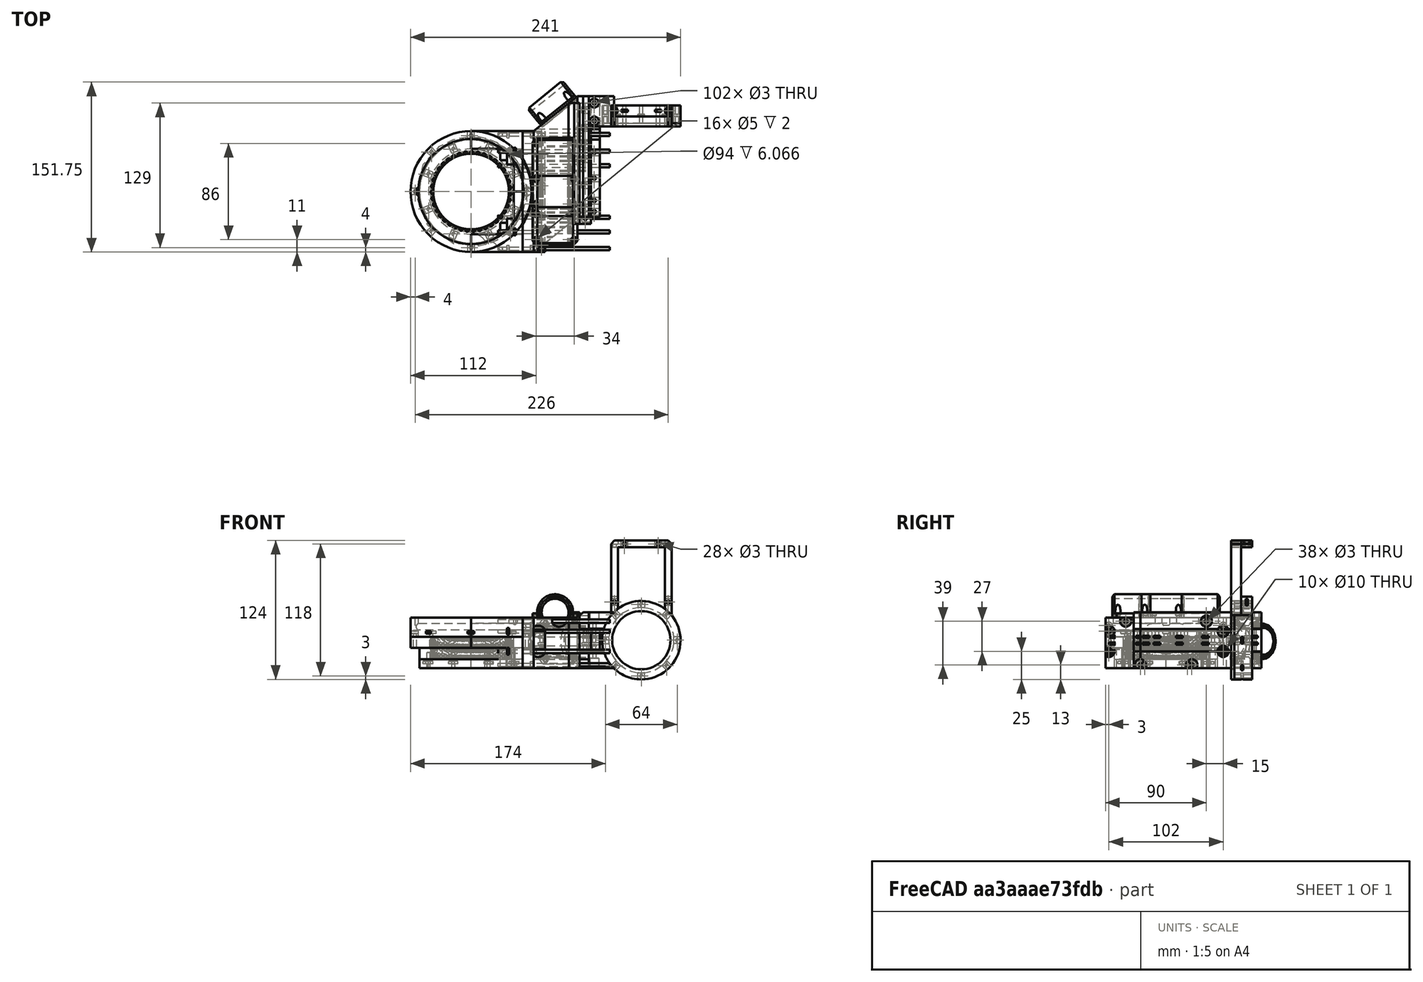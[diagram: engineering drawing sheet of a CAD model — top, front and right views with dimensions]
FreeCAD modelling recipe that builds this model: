
FCSTD DOCUMENT  (FreeCAD 0.19R24276 (Git))
Label: G-midi_adaptor-subshifted_022
License: All rights reserved
LicenseURL: http://en.wikipedia.org/wiki/All_rights_reserved
objects: Part::Cylinder×290, Part::Box×139, Part::Compound×113, Part::Cut×99, Part::Chamfer×16, Part::FeaturePython×11, Sketcher::SketchObject×2, Part::Extrusion×2, Part::Torus×2, Part::Fillet×2, Mesh::Feature×2, Part::Mirroring×1
note: 677 computed .brp shape members not serialized (recipe doc carries the construction recipe); baked Part::Feature solids carry a one-line shape summary decoded from their .brp

FEATURE [Part::Cylinder] Cylinder265  label="Válec265"
  Angle = 360
  AttacherType = Attacher::AttachEngine3D
  Height = 20
  Placement = pos=(45,19,-5) rot=(0,1,0;1.5708rad)
  Radius = 1.5
FEATURE [Part::Cylinder] Cylinder266  label="Válec266"
  Angle = 360
  AttacherType = Attacher::AttachEngine3D
  Height = 20
  Placement = pos=(45,-19,-5) rot=(0,1,0;1.5708rad)
  Radius = 1.5
FEATURE [Part::Cylinder] Cylinder267  label="Válec267"
  Angle = 360
  AttacherType = Attacher::AttachEngine3D
  Height = 20
  Placement = pos=(45,51,7) rot=(0,1,0;1.5708rad)
  Radius = 1.5
FEATURE [Part::Cylinder] Cylinder268  label="Válec268"
  Angle = 360
  AttacherType = Attacher::AttachEngine3D
  Height = 20
  Placement = pos=(45,-51,7) rot=(0,1,0;1.5708rad)
  Radius = 1.5
FEATURE [Part::Cylinder] Cylinder269  label="Válec269"
  Angle = 360
  AttacherType = Attacher::AttachEngine3D
  Height = 20
  Placement = pos=(45,-51,30) rot=(0,1,0;1.5708rad)
  Radius = 1.5
FEATURE [Part::Cylinder] Cylinder270  label="Válec270"
  Angle = 360
  AttacherType = Attacher::AttachEngine3D
  Height = 20
  Placement = pos=(45,51,30) rot=(0,1,0;1.5708rad)
  Radius = 1.5
FEATURE [Part::Cylinder] Cylinder271  label="Válec271"
  Angle = 360
  AttacherType = Attacher::AttachEngine3D
  Height = 28
  Placement = pos=(0,0,9) rot=(0,0,1;0rad)
  Radius = 54.5
FEATURE [Part::Box] Box117  label="Krychle117"
  AttacherType = Attacher::AttachEngine3D
  Height = 45
  Length = 10
  Placement = pos=(46,-54,-8) rot=(0,0,1;0rad)
  Width = 108
FEATURE [Part::Cylinder] Cylinder272  label="Válec272"
  Angle = 360
  AttacherType = Attacher::AttachEngine3D
  Height = 3
  Placement = pos=(53,51,30) rot=(0,1,0;1.5708rad)
  Radius = 3
FEATURE [Part::Cylinder] Cylinder273  label="Válec273"
  Angle = 360
  AttacherType = Attacher::AttachEngine3D
  Height = 3
  Placement = pos=(53,-51,30) rot=(0,1,0;1.5708rad)
  Radius = 3
FEATURE [Part::Cylinder] Cylinder274  label="Válec274"
  Angle = 360
  AttacherType = Attacher::AttachEngine3D
  Height = 3
  Placement = pos=(53,-51,7) rot=(0,1,0;1.5708rad)
  Radius = 3
FEATURE [Part::Cylinder] Cylinder275  label="Válec275"
  Angle = 360
  AttacherType = Attacher::AttachEngine3D
  Height = 3
  Placement = pos=(53,51,7) rot=(0,1,0;1.5708rad)
  Radius = 3
FEATURE [Part::Compound] Compound575
  Links = -> [Cylinder265,Cylinder266,Cylinder267,Cylinder268,Cylinder269,Cylinder270]
FEATURE [Part::Cylinder] Cylinder276  label="Válec276"
  Angle = 360
  AttacherType = Attacher::AttachEngine3D
  Height = 3
  Placement = pos=(53,-19,-5) rot=(0,1,0;1.5708rad)
  Radius = 3
FEATURE [Part::Cylinder] Cylinder277  label="Válec277"
  Angle = 360
  AttacherType = Attacher::AttachEngine3D
  Height = 3
  Placement = pos=(53,19,-5) rot=(0,1,0;1.5708rad)
  Radius = 3
FEATURE [Part::Compound] Compound576
  Links = -> [Cylinder277,Cylinder276,Cylinder275,Cylinder274,Cylinder273,Cylinder272]
FEATURE [Part::Cut] Cut348
  Base = -> Box117
  Tool = -> Compound576
FEATURE [Part::Cut] Cut349
  Base = -> Cut348
  Tool = -> Compound575
FEATURE [Part::Cut] Cut350
  Base = -> Cut349
  Tool = -> Cylinder271
FEATURE [Part::Cylinder] Cylinder278  label="Válec278"
  Angle = 360
  AttacherType = Attacher::AttachEngine3D
  Height = 50
  Placement = pos=(63,18,-12) rot=(0,0,1;0rad)
  Radius = 1.5
FEATURE [Part::Cylinder] Cylinder279  label="Válec279"
  Angle = 360
  AttacherType = Attacher::AttachEngine3D
  Height = 50
  Placement = pos=(63,33,-12) rot=(0,0,1;0rad)
  Radius = 1.5
FEATURE [Part::Cylinder] Cylinder280  label="Válec280"
  Angle = 360
  AttacherType = Attacher::AttachEngine3D
  Height = 50
  Placement = pos=(63,49,-12) rot=(0,0,1;0rad)
  Radius = 1.5
FEATURE [Part::Compound] Compound578
  Links = -> [Cylinder278,Cylinder279,Cylinder280]
FEATURE [Part::Box] Box118  label="Krychle118"
  AttacherType = Attacher::AttachEngine3D
  Height = 16
  Length = 10
  Placement = pos=(56,-54,6) rot=(0,0,1;0rad)
  Width = 108
FEATURE [Part::Box] Box119  label="Krychle119"
  AttacherType = Attacher::AttachEngine3D
  Height = 2
  Length = 6
  Placement = pos=(60,15,10) rot=(0,0,1;0rad)
  Width = 6
FEATURE [Part::Box] Box120  label="Krychle120"
  AttacherType = Attacher::AttachEngine3D
  Height = 2
  Length = 6
  Placement = pos=(60,30,10) rot=(0,0,1;0rad)
  Width = 6
FEATURE [Part::Box] Box121  label="Krychle121"
  AttacherType = Attacher::AttachEngine3D
  Height = 2
  Length = 6
  Placement = pos=(60,46,10) rot=(0,0,1;0rad)
  Width = 6
FEATURE [Part::Box] Box122  label="Krychle122"
  AttacherType = Attacher::AttachEngine3D
  Height = 2
  Length = 6
  Placement = pos=(60,15,16) rot=(0,0,1;0rad)
  Width = 6
FEATURE [Part::Box] Box123  label="Krychle123"
  AttacherType = Attacher::AttachEngine3D
  Height = 2
  Length = 6
  Placement = pos=(60,30,16) rot=(0,0,1;0rad)
  Width = 6
FEATURE [Part::Box] Box124  label="Krychle124"
  AttacherType = Attacher::AttachEngine3D
  Height = 2
  Length = 6
  Placement = pos=(60,46,16) rot=(0,0,1;0rad)
  Width = 6
FEATURE [Part::Compound] Compound577
  Links = -> [Box119,Box120,Box121,Box122,Box123,Box124]
FEATURE [Part::Cut] Cut351
  Base = -> Box118
  Tool = -> Compound577
FEATURE [Part::Cut] Cut352
  Base = -> Cut351
  Tool = -> Compound578
FEATURE [Part::Cylinder] Cylinder281  label="Válec281"
  Angle = 360
  AttacherType = Attacher::AttachEngine3D
  Height = 50
  Placement = pos=(63,5,-12) rot=(0,0,1;0rad)
  Radius = 1.5
FEATURE [Part::Cylinder] Cylinder282  label="Válec282"
  Angle = 360
  AttacherType = Attacher::AttachEngine3D
  Height = 50
  Placement = pos=(63,-22,-12) rot=(0,0,1;0rad)
  Radius = 1.5
FEATURE [Part::Cylinder] Cylinder283  label="Válec283"
  Angle = 360
  AttacherType = Attacher::AttachEngine3D
  Height = 50
  Placement = pos=(63,-33,-12) rot=(0,0,1;0rad)
  Radius = 1.5
FEATURE [Part::Cylinder] Cylinder284  label="Válec284"
  Angle = 360
  AttacherType = Attacher::AttachEngine3D
  Height = 50
  Placement = pos=(63,-48,-12) rot=(0,0,1;0rad)
  Radius = 1.5
FEATURE [Part::Compound] Compound580
  Links = -> [Cylinder281,Cylinder282,Cylinder283,Cylinder284]
FEATURE [Part::Box] Box125  label="Krychle125"
  AttacherType = Attacher::AttachEngine3D
  Height = 2
  Length = 6
  Placement = pos=(60,2,10) rot=(0,0,1;0rad)
  Width = 6
FEATURE [Part::Box] Box126  label="Krychle126"
  AttacherType = Attacher::AttachEngine3D
  Height = 2
  Length = 6
  Placement = pos=(60,2,16) rot=(0,0,1;0rad)
  Width = 6
FEATURE [Part::Box] Box127  label="Krychle127"
  AttacherType = Attacher::AttachEngine3D
  Height = 2
  Length = 6
  Placement = pos=(60,-25,10) rot=(0,0,1;0rad)
  Width = 6
FEATURE [Part::Box] Box128  label="Krychle128"
  AttacherType = Attacher::AttachEngine3D
  Height = 2
  Length = 6
  Placement = pos=(60,-25,16) rot=(0,0,1;0rad)
  Width = 6
FEATURE [Part::Box] Box129  label="Krychle129"
  AttacherType = Attacher::AttachEngine3D
  Height = 2
  Length = 6
  Placement = pos=(60,-36,10) rot=(0,0,1;0rad)
  Width = 6
FEATURE [Part::Box] Box130  label="Krychle130"
  AttacherType = Attacher::AttachEngine3D
  Height = 2
  Length = 6
  Placement = pos=(60,-36,16) rot=(0,0,1;0rad)
  Width = 6
FEATURE [Part::Box] Box131  label="Krychle131"
  AttacherType = Attacher::AttachEngine3D
  Height = 2
  Length = 6
  Placement = pos=(60,-51,10) rot=(0,0,1;0rad)
  Width = 6
FEATURE [Part::Box] Box132  label="Krychle132"
  AttacherType = Attacher::AttachEngine3D
  Height = 2
  Length = 6
  Placement = pos=(60,-51,16) rot=(0,0,1;0rad)
  Width = 6
FEATURE [Part::Compound] Compound579
  Links = -> [Box125,Box126,Box127,Box128,Box129,Box130,Box131,Box132]
FEATURE [Part::Cylinder] Cylinder285  label="Válec285"
  Angle = 360
  AttacherType = Attacher::AttachEngine3D
  Height = 16
  Placement = pos=(53,-51,7) rot=(0,1,0;1.5708rad)
  Radius = 3
FEATURE [Part::Cylinder] Cylinder286  label="Válec286"
  Angle = 360
  AttacherType = Attacher::AttachEngine3D
  Height = 16
  Placement = pos=(53,51,7) rot=(0,1,0;1.5708rad)
  Radius = 3
FEATURE [Part::Cylinder] Cylinder287  label="Válec287"
  Angle = 360
  AttacherType = Attacher::AttachEngine3D
  Height = 4
  Placement = pos=(50,0,5) rot=(0,0,1;0rad)
  Radius = 4
FEATURE [Part::Cut] Cut353
  Base = -> Cut352
  Tool = -> Compound579
FEATURE [Part::Cut] Cut354
  Base = -> Cut353
  Placement = pos=(0,0,3) rot=(0,0,1;0rad)
  Tool = -> Compound580
FEATURE [Part::Cut] Cut355
  Base = -> Cut354
  Tool = -> Cylinder285
FEATURE [Part::Cut] Cut356
  Base = -> Cut355
  Tool = -> Cylinder286
FEATURE [Part::Compound] Compound581  label="adapto_midi_podloch003"
  Links = -> [Cut356,Cut350]
FEATURE [Part::Cut] Cut357  label="G-midi_adaptor-high"
  Base = -> Compound581
  Tool = -> Cylinder287
FEATURE [Part::Cylinder] Cylinder288  label="Válec288"
  Angle = 360
  AttacherType = Attacher::AttachEngine3D
  Height = 20
  Placement = pos=(45,19,-5) rot=(0,1,0;1.5708rad)
  Radius = 1.5
FEATURE [Part::Cylinder] Cylinder289  label="Válec289"
  Angle = 360
  AttacherType = Attacher::AttachEngine3D
  Height = 20
  Placement = pos=(45,-19,-5) rot=(0,1,0;1.5708rad)
  Radius = 1.5
FEATURE [Part::Cylinder] Cylinder290  label="Válec290"
  Angle = 360
  AttacherType = Attacher::AttachEngine3D
  Height = 20
  Placement = pos=(45,51,7) rot=(0,1,0;1.5708rad)
  Radius = 1.5
FEATURE [Part::Cylinder] Cylinder291  label="Válec291"
  Angle = 360
  AttacherType = Attacher::AttachEngine3D
  Height = 20
  Placement = pos=(45,-51,7) rot=(0,1,0;1.5708rad)
  Radius = 1.5
FEATURE [Part::Cylinder] Cylinder292  label="Válec292"
  Angle = 360
  AttacherType = Attacher::AttachEngine3D
  Height = 20
  Placement = pos=(45,-51,30) rot=(0,1,0;1.5708rad)
  Radius = 1.5
FEATURE [Part::Cylinder] Cylinder293  label="Válec293"
  Angle = 360
  AttacherType = Attacher::AttachEngine3D
  Height = 20
  Placement = pos=(45,51,30) rot=(0,1,0;1.5708rad)
  Radius = 1.5
FEATURE [Part::Compound] Compound582
  Links = -> [Cylinder288,Cylinder289,Cylinder290,Cylinder291,Cylinder292,Cylinder293]
FEATURE [Part::Cylinder] Cylinder294  label="Válec294"
  Angle = 360
  AttacherType = Attacher::AttachEngine3D
  Height = 28
  Placement = pos=(0,0,9) rot=(0,0,1;0rad)
  Radius = 54.5
FEATURE [Part::Box] Box133  label="Krychle133"
  AttacherType = Attacher::AttachEngine3D
  Height = 45
  Length = 10
  Placement = pos=(46,-54,-8) rot=(0,0,1;0rad)
  Width = 108
FEATURE [Part::Cylinder] Cylinder295  label="Válec295"
  Angle = 360
  AttacherType = Attacher::AttachEngine3D
  Height = 3
  Placement = pos=(53,51,30) rot=(0,1,0;1.5708rad)
  Radius = 3
FEATURE [Part::Cylinder] Cylinder296  label="Válec296"
  Angle = 360
  AttacherType = Attacher::AttachEngine3D
  Height = 3
  Placement = pos=(53,-51,30) rot=(0,1,0;1.5708rad)
  Radius = 3
FEATURE [Part::Cylinder] Cylinder297  label="Válec297"
  Angle = 360
  AttacherType = Attacher::AttachEngine3D
  Height = 3
  Placement = pos=(53,-51,7) rot=(0,1,0;1.5708rad)
  Radius = 3
FEATURE [Part::Cylinder] Cylinder298  label="Válec298"
  Angle = 360
  AttacherType = Attacher::AttachEngine3D
  Height = 3
  Placement = pos=(53,51,7) rot=(0,1,0;1.5708rad)
  Radius = 3
FEATURE [Part::Cylinder] Cylinder299  label="Válec299"
  Angle = 360
  AttacherType = Attacher::AttachEngine3D
  Height = 3
  Placement = pos=(53,-19,-5) rot=(0,1,0;1.5708rad)
  Radius = 3
FEATURE [Part::Cylinder] Cylinder300  label="Válec300"
  Angle = 360
  AttacherType = Attacher::AttachEngine3D
  Height = 3
  Placement = pos=(53,19,-5) rot=(0,1,0;1.5708rad)
  Radius = 3
FEATURE [Part::Compound] Compound583
  Links = -> [Cylinder300,Cylinder299,Cylinder298,Cylinder297,Cylinder296,Cylinder295]
FEATURE [Part::Cut] Cut358
  Base = -> Box133
  Tool = -> Compound583
FEATURE [Part::Cut] Cut360
  Base = -> Cut358
  Tool = -> Compound582
FEATURE [Part::Cut] Cut359
  Base = -> Cut360
  Tool = -> Cylinder294
FEATURE [Sketcher::SketchObject] Sketch
  FullyConstrained = true
  Placement = pos=(0,-54,-8) rot=(0.57735,0.57735,0.57735;2.0944rad)
  sketch-geometry (4):
    g0: LineSegment StartX=0 StartY=0 StartZ=0 EndX=108 EndY=0 EndZ=0
    g1: LineSegment StartX=108 StartY=0 StartZ=0 EndX=108 EndY=45 EndZ=0
    g2: LineSegment StartX=108 StartY=45 StartZ=0 EndX=0 EndY=45 EndZ=0
    g3: LineSegment StartX=0 StartY=45 StartZ=0 EndX=0 EndY=0 EndZ=0
  constraints (11):
    c: Coincident(g0,g1)
    c: Coincident(g1,g2)
    c: Coincident(g2,g3)
    c: Coincident(g3,g0)
    c: Horizontal(g0)
    c: Horizontal(g2)
    c: Vertical(g1)
    c: Vertical(g3)
    c: Distance(g1) = 45
    c: Distance(g2) = 108
    c: Coincident(g-1,g0)
FEATURE [Part::Extrusion] Extrude
  Base = -> Sketch
  Dir = (1,0.8,0)
  DirMode = 0
  FaceMakerClass = Part::FaceMakerBullseye
  LengthFwd = 40
  LengthRev = 0
  Placement = pos=(56,0,0) rot=(0,0,1;0rad)
  Solid = true
  Symmetric = false
FEATURE [Part::Box] Box134  label="Krychle134"
  AttacherType = Attacher::AttachEngine3D
  Height = 50
  Length = 10
  Placement = pos=(87,-29,-8) rot=(0,0,1;0rad)
  Width = 108
FEATURE [Part::Torus] Torus004  label="Anuloid004"
  Angle1 = -180
  Angle2 = 180
  Angle3 = 360
  AttacherType = Attacher::AttachEngine3D
  Placement = pos=(0,0,29) rot=(0,0,1;0rad)
  Radius1 = 46
  Radius2 = 3.1
FEATURE [Part::Torus] Torus005  label="Anuloid005"
  Angle1 = -180
  Angle2 = 180
  Angle3 = 360
  AttacherType = Attacher::AttachEngine3D
  Placement = pos=(0,0,29) rot=(0,0,1;0rad)
  Radius1 = 46
  Radius2 = 3.1
FEATURE [Part::FeaturePython] wormgear024  # WARN: FeaturePython — macro-defined, semantics opaque (R4)
  AttacherType = Attacher::AttachEngine3D
  beta = 29.0893
  clearance = 0.25
  diameter = 70.1
  head = 0
  height = 20
  module = 1
  pressure_angle = 20
  reverse_pitch = false
  teeth = 39
  version = 0.0.3
FEATURE [Part::FeaturePython] wormgear025  # WARN: FeaturePython — macro-defined, semantics opaque (R4)
  AttacherType = Attacher::AttachEngine3D
  Placement = pos=(0,0,0) rot=(0,0,-1;0.005411rad)
  beta = 29.0893
  clearance = 0.25
  diameter = 70.1
  head = 0
  height = 20
  module = 1
  pressure_angle = 20
  reverse_pitch = true
  teeth = 39
  version = 0.0.3
FEATURE [Part::Cylinder] Cylinder113  label="Válec113"
  Angle = 360
  AttacherType = Attacher::AttachEngine3D
  Height = 10
  Radius = 54
FEATURE [Part::Cut] Cut063
  Base = -> Cylinder113
  Placement = pos=(0,0,10) rot=(0,0,1;0.034907rad)
  Tool = -> wormgear025
FEATURE [Part::Cylinder] Cylinder114  label="Válec114"
  Angle = 360
  AttacherType = Attacher::AttachEngine3D
  Height = 10
  Radius = 46
FEATURE [Part::Cut] Cut062
  Base = -> Cylinder114
  Tool = -> wormgear024
FEATURE [Part::Compound] Compound191
  Links = -> [Cut063,Cut062]
FEATURE [Part::Box] Box070  label="Krychle070"
  AttacherType = Attacher::AttachEngine3D
  Height = 2
  Length = 8
  Placement = pos=(37,-3,-4) rot=(0,0,1;0rad)
  Width = 6
FEATURE [Part::FeaturePython] Tube009  # WARN: FeaturePython — macro-defined, semantics opaque (R4)
  AttacherType = Attacher::AttachEngine3D
  Height = 8
  InnerRadius = 38
  OuterRadius = 46
  Placement = pos=(0,0,-8) rot=(0,0,1;0rad)
FEATURE [Part::Cylinder] Cylinder189  label="Válec189"
  Angle = 360
  AttacherType = Attacher::AttachEngine3D
  Height = 60
  Placement = pos=(41,0,-54) rot=(0,0,1;0rad)
  Radius = 1.5
FEATURE [Part::Cylinder] Cylinder190  label="Válec190"
  Angle = 360
  AttacherType = Attacher::AttachEngine3D
  Height = 40
  Placement = pos=(256,0,-30) rot=(0,0,1;0rad)
  Radius = 10
FEATURE [Part::Box] Box071  label="Krychle071"
  AttacherType = Attacher::AttachEngine3D
  Height = 28
  Length = 8
  Placement = pos=(238,0,-8) rot=(0,0,1;0rad)
  Width = 38
FEATURE [Part::Cylinder] Cylinder191  label="Válec191"
  Angle = 360
  AttacherType = Attacher::AttachEngine3D
  Height = 40
  Placement = pos=(214,56,-30) rot=(0,0,1;0rad)
  Radius = 12
FEATURE [Part::Compound] Compound193
  Links = -> [Cylinder190,Cylinder191]
FEATURE [Part::Box] Box072  label="Krychle072"
  AttacherType = Attacher::AttachEngine3D
  Height = 28
  Length = 46
  Placement = pos=(200,38,-8) rot=(0,0,1;0rad)
  Width = 16
FEATURE [Part::Compound] Compound192
  Links = -> [Box071,Box072]
FEATURE [Part::Cut] Cut065
  Base = -> Compound192
  Tool = -> Compound193
FEATURE [Part::Cylinder] Cylinder192  label="Válec192"
  Angle = 360
  AttacherType = Attacher::AttachEngine3D
  Height = 40
  Placement = pos=(202,50,-30) rot=(0,0,1;0rad)
  Radius = 12
FEATURE [Part::Cut] Cut066
  Base = -> Cut065
  Placement = pos=(-200,0,0) rot=(0,0,1;0rad)
  Tool = -> Cylinder192
FEATURE [Part::Box] Box073  label="Krychle073"
  AttacherType = Attacher::AttachEngine3D
  Height = 28
  Length = 6
  Placement = pos=(26,28,-8) rot=(0,0,1;0rad)
  Width = 10
FEATURE [Part::Box] Box074  label="Krychle074"
  AttacherType = Attacher::AttachEngine3D
  Height = 28
  Length = 6
  Placement = pos=(32,24,-8) rot=(0,0,1;0rad)
  Width = 14
FEATURE [Part::Compound] Compound
  Links = -> [Box073,Box074]
FEATURE [Part::Compound] Compound194
  Links = -> [Cut066,Compound]
FEATURE [Part::Box] Box075  label="Krychle075"
  AttacherType = Attacher::AttachEngine3D
  Height = 28
  Length = 8
  Placement = pos=(238,0,-8) rot=(0,0,1;0rad)
  Width = 38
FEATURE [Part::Cylinder] Cylinder193  label="Válec193"
  Angle = 360
  AttacherType = Attacher::AttachEngine3D
  Height = 40
  Placement = pos=(214,56,-30) rot=(0,0,1;0rad)
  Radius = 12
FEATURE [Part::Cylinder] Cylinder194  label="Válec194"
  Angle = 360
  AttacherType = Attacher::AttachEngine3D
  Height = 40
  Placement = pos=(256,0,-30) rot=(0,0,1;0rad)
  Radius = 10
FEATURE [Part::Compound] Compound198
  Links = -> [Cylinder194,Cylinder193]
FEATURE [Part::Box] Box076  label="Krychle076"
  AttacherType = Attacher::AttachEngine3D
  Height = 28
  Length = 6
  Placement = pos=(26,28,-8) rot=(0,0,1;0rad)
  Width = 10
FEATURE [Part::Cylinder] Cylinder195  label="Válec195"
  Angle = 360
  AttacherType = Attacher::AttachEngine3D
  Height = 40
  Placement = pos=(202,50,-30) rot=(0,0,1;0rad)
  Radius = 12
FEATURE [Part::Box] Box077  label="Krychle077"
  AttacherType = Attacher::AttachEngine3D
  Height = 28
  Length = 6
  Placement = pos=(32,24,-8) rot=(0,0,1;0rad)
  Width = 14
FEATURE [Part::Compound] Compound195
  Links = -> [Box076,Box077]
FEATURE [Part::Box] Box078  label="Krychle078"
  AttacherType = Attacher::AttachEngine3D
  Height = 28
  Length = 46
  Placement = pos=(200,38,-8) rot=(0,0,1;0rad)
  Width = 16
FEATURE [Part::Compound] Compound197
  Links = -> [Box075,Box078]
FEATURE [Part::Cut] Cut068
  Base = -> Compound197
  Tool = -> Compound198
FEATURE [Part::Cut] Cut067
  Base = -> Cut068
  Placement = pos=(-200,0,0) rot=(0,0,1;0rad)
  Tool = -> Cylinder195
FEATURE [Part::Compound] Compound196
  Links = -> [Cut067,Compound195]
FEATURE [Part::Mirroring] mirror  label="Compound196 (mirrored)"
  Base = (0,0,0)
  Normal = (1e-16,-1,0)
  Source = -> Compound196
FEATURE [Part::Box] Box087  label="Krychle087"
  AttacherType = Attacher::AttachEngine3D
  Height = 2
  Length = 8
  Placement = pos=(28.2843,24.0416,-4) rot=(0,0,1;0.785398rad)
  Width = 6
FEATURE [Part::Box] Box088  label="Krychle088"
  AttacherType = Attacher::AttachEngine3D
  Height = 2
  Length = 8
  Placement = pos=(3,37,-4) rot=(0,0,1;1.5708rad)
  Width = 6
FEATURE [Part::Box] Box089  label="Krychle089"
  AttacherType = Attacher::AttachEngine3D
  Height = 2
  Length = 8
  Placement = pos=(-24.0416,28.2843,-4) rot=(0,0,1;2.35619rad)
  Width = 6
FEATURE [Part::Box] Box090  label="Krychle090"
  AttacherType = Attacher::AttachEngine3D
  Height = 2
  Length = 8
  Placement = pos=(-37,3,-4) rot=(0,0,1;3.14159rad)
  Width = 6
FEATURE [Part::Box] Box091  label="Krychle091"
  AttacherType = Attacher::AttachEngine3D
  Height = 2
  Length = 8
  Placement = pos=(-28.2843,-24.0416,-4) rot=(0,0,1;3.92699rad)
  Width = 6
FEATURE [Part::Box] Box092  label="Krychle092"
  AttacherType = Attacher::AttachEngine3D
  Height = 2
  Length = 8
  Placement = pos=(-3,-37,-4) rot=(0,0,-1;1.5708rad)
  Width = 6
FEATURE [Part::Box] Box093  label="Krychle093"
  AttacherType = Attacher::AttachEngine3D
  Height = 2
  Length = 8
  Placement = pos=(24.0416,-28.2843,-4) rot=(0,0,-1;0.785398rad)
  Width = 6
FEATURE [Part::Cylinder] Cylinder204  label="Válec204"
  Angle = 360
  AttacherType = Attacher::AttachEngine3D
  Height = 60
  Placement = pos=(28.9914,28.9914,-54) rot=(0,0,1;0.785398rad)
  Radius = 1.5
FEATURE [Part::Cylinder] Cylinder205  label="Válec205"
  Angle = 360
  AttacherType = Attacher::AttachEngine3D
  Height = 60
  Placement = pos=(-4e-15,41,-54) rot=(0,0,1;1.5708rad)
  Radius = 1.5
FEATURE [Part::Cylinder] Cylinder206  label="Válec206"
  Angle = 360
  AttacherType = Attacher::AttachEngine3D
  Height = 60
  Placement = pos=(-28.9914,28.9914,-54) rot=(0,0,1;2.35619rad)
  Radius = 1.5
FEATURE [Part::Cylinder] Cylinder207  label="Válec207"
  Angle = 360
  AttacherType = Attacher::AttachEngine3D
  Height = 60
  Placement = pos=(-41,-1.1e-14,-54) rot=(0,0,1;3.14159rad)
  Radius = 1.5
FEATURE [Part::Compound] Compound206
  Links = -> [Box087,Box088,Box089,Box090,Box091,Box092,Box093,Box070]
  Placement = pos=(0,0,0) rot=(0,0,1;0.392699rad)
FEATURE [Part::Compound] Compound210
  Links = -> [mirror,Compound194]
FEATURE [Part::Cylinder] Cylinder208  label="Válec208"
  Angle = 360
  AttacherType = Attacher::AttachEngine3D
  Height = 60
  Placement = pos=(-28.9914,-28.9914,-54) rot=(0,0,1;3.92699rad)
  Radius = 1.5
FEATURE [Part::Cylinder] Cylinder209  label="Válec209"
  Angle = 360
  AttacherType = Attacher::AttachEngine3D
  Height = 60
  Placement = pos=(1.2e-14,-41,-54) rot=(0,0,-1;1.5708rad)
  Radius = 1.5
FEATURE [Part::Cylinder] Cylinder210  label="Válec210"
  Angle = 360
  AttacherType = Attacher::AttachEngine3D
  Height = 60
  Placement = pos=(28.9914,-28.9914,-54) rot=(0,0,-1;0.785398rad)
  Radius = 1.5
FEATURE [Part::Compound] Compound207
  Links = -> [Cylinder204,Cylinder205,Cylinder206,Cylinder207,Cylinder208,Cylinder209,Cylinder210,Cylinder189]
  Placement = pos=(0,0,0) rot=(0,0,1;0.392699rad)
FEATURE [Part::Cut] Cut069
  Base = -> Tube009
  Tool = -> Compound207
FEATURE [Part::Cut] Cut070
  Base = -> Cut069
  Tool = -> Compound206
FEATURE [Part::Cylinder] Cylinder211  label="Válec211"
  Angle = 360
  AttacherType = Attacher::AttachEngine3D
  Height = 60
  Placement = pos=(28.9914,-28.9914,-54) rot=(0,0,-1;0.785398rad)
  Radius = 1.5
FEATURE [Part::Cylinder] Cylinder212  label="Válec212"
  Angle = 360
  AttacherType = Attacher::AttachEngine3D
  Height = 60
  Placement = pos=(-4e-15,41,-54) rot=(0,0,1;1.5708rad)
  Radius = 1.5
FEATURE [Part::Cylinder] Cylinder213  label="Válec213"
  Angle = 360
  AttacherType = Attacher::AttachEngine3D
  Height = 60
  Placement = pos=(-28.9914,28.9914,-54) rot=(0,0,1;2.35619rad)
  Radius = 1.5
FEATURE [Part::Cylinder] Cylinder214  label="Válec214"
  Angle = 360
  AttacherType = Attacher::AttachEngine3D
  Height = 60
  Placement = pos=(28.9914,28.9914,-54) rot=(0,0,1;0.785398rad)
  Radius = 1.5
FEATURE [Part::Cylinder] Cylinder215  label="Válec215"
  Angle = 360
  AttacherType = Attacher::AttachEngine3D
  Height = 60
  Placement = pos=(-41,-1.1e-14,-54) rot=(0,0,1;3.14159rad)
  Radius = 1.5
FEATURE [Part::Cylinder] Cylinder216  label="Válec216"
  Angle = 360
  AttacherType = Attacher::AttachEngine3D
  Height = 60
  Placement = pos=(-28.9914,-28.9914,-54) rot=(0,0,1;3.92699rad)
  Radius = 1.5
FEATURE [Part::Cylinder] Cylinder217  label="Válec217"
  Angle = 360
  AttacherType = Attacher::AttachEngine3D
  Height = 60
  Placement = pos=(1.2e-14,-41,-54) rot=(0,0,-1;1.5708rad)
  Radius = 1.5
FEATURE [Part::Cylinder] Cylinder218  label="Válec218"
  Angle = 360
  AttacherType = Attacher::AttachEngine3D
  Height = 60
  Placement = pos=(41,0,-54) rot=(0,0,1;0rad)
  Radius = 1.5
FEATURE [Part::Compound] Compound208
  Links = -> [Cylinder214,Cylinder212,Cylinder213,Cylinder215,Cylinder216,Cylinder217,Cylinder211,Cylinder218]
  Placement = pos=(0,0,0) rot=(0,0,1;0.392699rad)
FEATURE [Part::Box] Box094  label="Krychle094"
  AttacherType = Attacher::AttachEngine3D
  Height = 2
  Length = 8
  Placement = pos=(3,37,-4) rot=(0,0,1;1.5708rad)
  Width = 6
FEATURE [Part::Box] Box095  label="Krychle095"
  AttacherType = Attacher::AttachEngine3D
  Height = 2
  Length = 8
  Placement = pos=(28.2843,24.0416,-4) rot=(0,0,1;0.785398rad)
  Width = 6
FEATURE [Part::Box] Box096  label="Krychle096"
  AttacherType = Attacher::AttachEngine3D
  Height = 2
  Length = 8
  Placement = pos=(24.0416,-28.2843,-4) rot=(0,0,-1;0.785398rad)
  Width = 6
FEATURE [Part::Box] Box097  label="Krychle097"
  AttacherType = Attacher::AttachEngine3D
  Height = 2
  Length = 8
  Placement = pos=(-37,3,-4) rot=(0,0,1;3.14159rad)
  Width = 6
FEATURE [Part::Box] Box098  label="Krychle098"
  AttacherType = Attacher::AttachEngine3D
  Height = 2
  Length = 8
  Placement = pos=(-28.2843,-24.0416,-4) rot=(0,0,1;3.92699rad)
  Width = 6
FEATURE [Part::Box] Box099  label="Krychle099"
  AttacherType = Attacher::AttachEngine3D
  Height = 2
  Length = 8
  Placement = pos=(-3,-37,-4) rot=(0,0,-1;1.5708rad)
  Width = 6
FEATURE [Part::Box] Box100  label="Krychle100"
  AttacherType = Attacher::AttachEngine3D
  Height = 2
  Length = 8
  Placement = pos=(-24.0416,28.2843,-4) rot=(0,0,1;2.35619rad)
  Width = 6
FEATURE [Part::Box] Box101  label="Krychle101"
  AttacherType = Attacher::AttachEngine3D
  Height = 2
  Length = 8
  Placement = pos=(37,-3,-4) rot=(0,0,1;0rad)
  Width = 6
FEATURE [Part::Compound] Compound209
  Links = -> [Box095,Box094,Box100,Box097,Box098,Box099,Box096,Box101]
  Placement = pos=(0,0,0) rot=(0,0,1;0.392699rad)
FEATURE [Part::Cylinder] Cylinder219  label="Válec219"
  Angle = 360
  AttacherType = Attacher::AttachEngine3D
  Height = 60
  Placement = pos=(28.9914,-28.9914,-54) rot=(0,0,-1;0.785398rad)
  Radius = 1.5
FEATURE [Part::Cylinder] Cylinder220  label="Válec220"
  Angle = 360
  AttacherType = Attacher::AttachEngine3D
  Height = 60
  Placement = pos=(-28.9914,28.9914,-54) rot=(0,0,1;2.35619rad)
  Radius = 1.5
FEATURE [Part::Cylinder] Cylinder221  label="Válec221"
  Angle = 360
  AttacherType = Attacher::AttachEngine3D
  Height = 60
  Placement = pos=(28.9914,28.9914,-54) rot=(0,0,1;0.785398rad)
  Radius = 1.5
FEATURE [Part::Cylinder] Cylinder222  label="Válec222"
  Angle = 360
  AttacherType = Attacher::AttachEngine3D
  Height = 60
  Placement = pos=(-4e-15,41,-54) rot=(0,0,1;1.5708rad)
  Radius = 1.5
FEATURE [Part::Cylinder] Cylinder223  label="Válec223"
  Angle = 360
  AttacherType = Attacher::AttachEngine3D
  Height = 60
  Placement = pos=(41,0,-54) rot=(0,0,1;0rad)
  Radius = 1.5
FEATURE [Part::Cut] Cut071
  Base = -> Compound210
  Tool = -> Compound209
FEATURE [Part::Cut] Cut072
  Base = -> Cut071
  Tool = -> Compound208
FEATURE [Part::Cylinder] Cylinder224  label="Válec224"
  Angle = 360
  AttacherType = Attacher::AttachEngine3D
  Height = 60
  Placement = pos=(-28.9914,-28.9914,-54) rot=(0,0,1;3.92699rad)
  Radius = 1.5
FEATURE [Part::Cylinder] Cylinder225  label="Válec225"
  Angle = 360
  AttacherType = Attacher::AttachEngine3D
  Height = 60
  Placement = pos=(-41,-1.1e-14,-54) rot=(0,0,1;3.14159rad)
  Radius = 1.5
FEATURE [Part::Cylinder] Cylinder226  label="Válec226"
  Angle = 360
  AttacherType = Attacher::AttachEngine3D
  Height = 60
  Placement = pos=(1.2e-14,-41,-54) rot=(0,0,-1;1.5708rad)
  Radius = 1.5
FEATURE [Part::Compound] Compound211
  Links = -> [Cylinder221,Cylinder222,Cylinder220,Cylinder225,Cylinder224,Cylinder226,Cylinder219,Cylinder223]
  Placement = pos=(0,0,0) rot=(0,0,1;0.392699rad)
FEATURE [Part::Cut] Cut073
  Base = -> Compound191
  Tool = -> Compound211
FEATURE [Part::Cylinder] Cylinder227  label="Válec227"
  Angle = 360
  AttacherType = Attacher::AttachEngine3D
  Height = 60
  Placement = pos=(28,-51,7) rot=(0,1,0;1.5708rad)
  Radius = 1.5
FEATURE [Part::Cylinder] Cylinder228  label="Válec228"
  Angle = 360
  AttacherType = Attacher::AttachEngine3D
  Height = 60
  Placement = pos=(28,51,7) rot=(0,1,0;1.5708rad)
  Radius = 1.5
FEATURE [Part::Cylinder] Cylinder229  label="Válec229"
  Angle = 360
  AttacherType = Attacher::AttachEngine3D
  Height = 60
  Placement = pos=(32,21,-5) rot=(0,1,0;1.5708rad)
  Radius = 1.5
FEATURE [Part::Cylinder] Cylinder230  label="Válec230"
  Angle = 360
  AttacherType = Attacher::AttachEngine3D
  Height = 60
  Placement = pos=(32,-21,-5) rot=(0,1,0;1.5708rad)
  Radius = 1.5
FEATURE [Part::Compound] Compound212
  Links = -> [Cylinder229,Cylinder230,Cylinder228,Cylinder227]
FEATURE [Part::Cut] Cut074
  Base = -> Cut073
  Tool = -> Compound212
FEATURE [Part::Box] Box102  label="Krychle102"
  AttacherType = Attacher::AttachEngine3D
  Height = 6
  Length = 2
  Placement = pos=(36,18,-8) rot=(0,0,1;0rad)
  Width = 6
FEATURE [Part::Box] Box103  label="Krychle103"
  AttacherType = Attacher::AttachEngine3D
  Height = 6
  Length = 2
  Placement = pos=(36,-24,-8) rot=(0,0,1;0rad)
  Width = 6
FEATURE [Part::Box] Box104  label="Krychle104"
  AttacherType = Attacher::AttachEngine3D
  Height = 6
  Length = 2
  Placement = pos=(32,-54,4) rot=(0,0,1;0rad)
  Width = 6
FEATURE [Part::Box] Box105  label="Krychle105"
  AttacherType = Attacher::AttachEngine3D
  Height = 6
  Length = 2
  Placement = pos=(32,48,4) rot=(0,0,1;0rad)
  Width = 6
FEATURE [Part::Compound] Compound213
  Links = -> [Box102,Box103,Box105,Box104]
FEATURE [Part::Cut] Cut075
  Base = -> Cut074
  Tool = -> Compound213
FEATURE [Part::Cylinder] Cylinder239  label="Válec239"
  Angle = 360
  AttacherType = Attacher::AttachEngine3D
  Height = 50
  Placement = pos=(50,0,-15) rot=(0,0,1;0rad)
  Radius = 1.5
FEATURE [Part::Cylinder] Cylinder240  label="Válec240"
  Angle = 360
  AttacherType = Attacher::AttachEngine3D
  Height = 50
  Placement = pos=(35.3553,35.3553,-15) rot=(0,0,1;0.785398rad)
  Radius = 1.5
FEATURE [Part::Cylinder] Cylinder241  label="Válec241"
  Angle = 360
  AttacherType = Attacher::AttachEngine3D
  Height = 50
  Placement = pos=(-7e-15,50,-15) rot=(0,0,1;1.5708rad)
  Radius = 1.5
FEATURE [Part::Cylinder] Cylinder242  label="Válec242"
  Angle = 360
  AttacherType = Attacher::AttachEngine3D
  Height = 50
  Placement = pos=(-35.3553,35.3553,-15) rot=(0,0,1;2.35619rad)
  Radius = 1.5
FEATURE [Part::Cylinder] Cylinder243  label="Válec243"
  Angle = 360
  AttacherType = Attacher::AttachEngine3D
  Height = 50
  Placement = pos=(-50,-2.3e-14,-15) rot=(0,0,1;3.14159rad)
  Radius = 1.5
FEATURE [Part::Cylinder] Cylinder244  label="Válec244"
  Angle = 360
  AttacherType = Attacher::AttachEngine3D
  Height = 50
  Placement = pos=(-35.3553,-35.3553,-15) rot=(0,0,1;3.92699rad)
  Radius = 1.5
FEATURE [Part::Cylinder] Cylinder245  label="Válec245"
  Angle = 360
  AttacherType = Attacher::AttachEngine3D
  Height = 50
  Placement = pos=(2.5e-14,-50,-15) rot=(0,0,-1;1.5708rad)
  Radius = 1.5
FEATURE [Part::Cylinder] Cylinder246  label="Válec246"
  Angle = 360
  AttacherType = Attacher::AttachEngine3D
  Height = 50
  Placement = pos=(35.3553,-35.3553,-15) rot=(0,0,-1;0.785398rad)
  Radius = 1.5
FEATURE [Part::Compound] Compound217
  Links = -> [Cylinder239,Cylinder240,Cylinder241,Cylinder242,Cylinder243,Cylinder244,Cylinder245,Cylinder246]
FEATURE [Part::Cut] Cut076
  Base = -> Cut075
  Tool = -> Compound217
FEATURE [Part::Box] Box106  label="Krychle106"
  AttacherType = Attacher::AttachEngine3D
  Height = 6
  Length = 2
  Placement = pos=(36,-26,-8) rot=(0,0,1;0rad)
  Width = 6
FEATURE [Part::Box] Box107  label="Krychle107"
  AttacherType = Attacher::AttachEngine3D
  Height = 6
  Length = 2
  Placement = pos=(32,-54,4) rot=(0,0,1;0rad)
  Width = 6
FEATURE [Part::Box] Box108  label="Krychle108"
  AttacherType = Attacher::AttachEngine3D
  Height = 6
  Length = 2
  Placement = pos=(36,20,-8) rot=(0,0,1;0rad)
  Width = 6
FEATURE [Part::Box] Box109  label="Krychle109"
  AttacherType = Attacher::AttachEngine3D
  Height = 6
  Length = 2
  Placement = pos=(32,48,4) rot=(0,0,1;0rad)
  Width = 6
FEATURE [Part::Compound] Compound218
  Links = -> [Box108,Box106,Box109,Box107]
FEATURE [Part::Cut] Cut080
  Base = -> Cut070
  Tool = -> Compound218
FEATURE [Part::Cylinder] Cylinder247  label="Válec247"
  Angle = 360
  AttacherType = Attacher::AttachEngine3D
  Height = 60
  Placement = pos=(32,-23,-5) rot=(0,1,0;1.5708rad)
  Radius = 1.5
FEATURE [Part::Cylinder] Cylinder248  label="Válec248"
  Angle = 360
  AttacherType = Attacher::AttachEngine3D
  Height = 60
  Placement = pos=(28,51,7) rot=(0,1,0;1.5708rad)
  Radius = 1.5
FEATURE [Part::Cylinder] Cylinder249  label="Válec249"
  Angle = 360
  AttacherType = Attacher::AttachEngine3D
  Height = 60
  Placement = pos=(32,23,-5) rot=(0,1,0;1.5708rad)
  Radius = 1.5
FEATURE [Part::Cylinder] Cylinder250  label="Válec250"
  Angle = 360
  AttacherType = Attacher::AttachEngine3D
  Height = 60
  Placement = pos=(28,-51,7) rot=(0,1,0;1.5708rad)
  Radius = 1.5
FEATURE [Part::Compound] Compound219
  Links = -> [Cylinder249,Cylinder247,Cylinder248,Cylinder250]
FEATURE [Part::Cylinder] Cylinder251  label="Válec251"
  Angle = 360
  AttacherType = Attacher::AttachEngine3D
  Height = 50
  Placement = pos=(35.3553,35.3553,-15) rot=(0,0,1;0.785398rad)
  Radius = 1.5
FEATURE [Part::Cylinder] Cylinder252  label="Válec252"
  Angle = 360
  AttacherType = Attacher::AttachEngine3D
  Height = 50
  Placement = pos=(50,0,-15) rot=(0,0,1;0rad)
  Radius = 1.5
FEATURE [Part::Cylinder] Cylinder253  label="Válec253"
  Angle = 360
  AttacherType = Attacher::AttachEngine3D
  Height = 50
  Placement = pos=(35.3553,-35.3553,-15) rot=(0,0,-1;0.785398rad)
  Radius = 1.5
FEATURE [Part::Cylinder] Cylinder254  label="Válec254"
  Angle = 360
  AttacherType = Attacher::AttachEngine3D
  Height = 50
  Placement = pos=(-50,-2.3e-14,-15) rot=(0,0,1;3.14159rad)
  Radius = 1.5
FEATURE [Part::Cylinder] Cylinder255  label="Válec255"
  Angle = 360
  AttacherType = Attacher::AttachEngine3D
  Height = 50
  Placement = pos=(2.5e-14,-50,-15) rot=(0,0,-1;1.5708rad)
  Radius = 1.5
FEATURE [Part::Cylinder] Cylinder256  label="Válec256"
  Angle = 360
  AttacherType = Attacher::AttachEngine3D
  Height = 50
  Placement = pos=(-35.3553,35.3553,-15) rot=(0,0,1;2.35619rad)
  Radius = 1.5
FEATURE [Part::Cylinder] Cylinder257  label="Válec257"
  Angle = 360
  AttacherType = Attacher::AttachEngine3D
  Height = 50
  Placement = pos=(-7e-15,50,-15) rot=(0,0,1;1.5708rad)
  Radius = 1.5
FEATURE [Part::Cylinder] Cylinder258  label="Válec258"
  Angle = 360
  AttacherType = Attacher::AttachEngine3D
  Height = 50
  Placement = pos=(-35.3553,-35.3553,-15) rot=(0,0,1;3.92699rad)
  Radius = 1.5
FEATURE [Part::Box] Box110  label="Krychle110"
  AttacherType = Attacher::AttachEngine3D
  Height = 6
  Length = 2
  Placement = pos=(36,20,-8) rot=(0,0,1;0rad)
  Width = 6
FEATURE [Part::Compound] Compound220
  Links = -> [Cylinder252,Cylinder251,Cylinder257,Cylinder256,Cylinder254,Cylinder258,Cylinder255,Cylinder253]
FEATURE [Part::Cut] Cut077
  Base = -> Cut072
  Tool = -> Compound220
FEATURE [Part::Box] Box111  label="Krychle111"
  AttacherType = Attacher::AttachEngine3D
  Height = 6
  Length = 2
  Placement = pos=(32,-54,4) rot=(0,0,1;0rad)
  Width = 6
FEATURE [Part::Box] Box112  label="Krychle112"
  AttacherType = Attacher::AttachEngine3D
  Height = 6
  Length = 2
  Placement = pos=(36,-26,-8) rot=(0,0,1;0rad)
  Width = 6
FEATURE [Part::Box] Box113  label="Krychle113"
  AttacherType = Attacher::AttachEngine3D
  Height = 6
  Length = 2
  Placement = pos=(32,48,4) rot=(0,0,1;0rad)
  Width = 6
FEATURE [Part::Compound] Compound221
  Links = -> [Box110,Box112,Box113,Box111]
FEATURE [Part::Cut] Cut078
  Base = -> Cut077
  Tool = -> Compound221
FEATURE [Part::Cylinder] Cylinder259  label="Válec259"
  Angle = 360
  AttacherType = Attacher::AttachEngine3D
  Height = 60
  Placement = pos=(28,51,7) rot=(0,1,0;1.5708rad)
  Radius = 1.5
FEATURE [Part::Cylinder] Cylinder260  label="Válec260"
  Angle = 360
  AttacherType = Attacher::AttachEngine3D
  Height = 60
  Placement = pos=(32,-23,-5) rot=(0,1,0;1.5708rad)
  Radius = 1.5
FEATURE [Part::Cylinder] Cylinder261  label="Válec261"
  Angle = 360
  AttacherType = Attacher::AttachEngine3D
  Height = 60
  Placement = pos=(32,23,-5) rot=(0,1,0;1.5708rad)
  Radius = 1.5
FEATURE [Part::Cylinder] Cylinder262  label="Válec262"
  Angle = 360
  AttacherType = Attacher::AttachEngine3D
  Height = 60
  Placement = pos=(28,-51,7) rot=(0,1,0;1.5708rad)
  Radius = 1.5
FEATURE [Part::Compound] Compound222
  Links = -> [Cylinder261,Cylinder260,Cylinder259,Cylinder262]
FEATURE [Part::Cut] Cut079
  Base = -> Cut078
  Tool = -> Compound222
FEATURE [Part::Cylinder] Cylinder263  label="Válec263"
  Angle = 360
  AttacherType = Attacher::AttachEngine3D
  Height = 50
  Placement = pos=(35.36,35.36,-40) rot=(0,0,1;0.785398rad)
  Radius = 4
FEATURE [Part::Cylinder] Cylinder264  label="Válec264"
  Angle = 360
  AttacherType = Attacher::AttachEngine3D
  Height = 50
  Placement = pos=(35.36,-35.36,-40) rot=(0,0,1;0.785398rad)
  Radius = 4
FEATURE [Part::Compound] Compound223
  Links = -> [Cylinder263,Cylinder264]
FEATURE [Part::Cut] Cut081
  Base = -> Cut080
  Tool = -> Compound219
FEATURE [Part::Cut] Cut082
  Base = -> Cut079
  Tool = -> Compound223
FEATURE [Part::Fillet] Fillet
  Base = -> Cut082
  Edges = 1 edges r=8: [Edge273]
FEATURE [Part::Fillet] Fillet020
  Base = -> Fillet
  Edges = 1 edges r=8: [Edge173]
FEATURE [Part::Compound] Compound224  label="J-midi_monoblok"
  Links = -> [Cut076,Cut081,Fillet020]
FEATURE [Part::FeaturePython] Tube002  # WARN: FeaturePython — macro-defined, semantics opaque (R4)
  AttacherType = Attacher::AttachEngine3D
  Height = 17
  InnerRadius = 47
  OuterRadius = 54
  Placement = pos=(0,0,20) rot=(0,0,1;0rad)
FEATURE [Part::Cylinder] Cylinder006  label="Válec006"
  Angle = 360
  AttacherType = Attacher::AttachEngine3D
  Height = 10
  Placement = pos=(-46.3,0,30) rot=(0,0,1;0rad)
  Radius = 3.5
FEATURE [Part::Box] Box156  label="Krychle156"
  AttacherType = Attacher::AttachEngine3D
  Height = 17
  Length = 46
  Placement = pos=(0,-54,20) rot=(0,0,1;0rad)
  Width = 108
FEATURE [Part::Box] Box157  label="Krychle157"
  AttacherType = Attacher::AttachEngine3D
  Height = 2
  Length = 8
  Placement = pos=(46,-3,23) rot=(0,0,1;0rad)
  Width = 6
FEATURE [Part::Box] Box158  label="Krychle158"
  AttacherType = Attacher::AttachEngine3D
  Height = 2
  Length = 8
  Placement = pos=(34.6482,30.4056,23) rot=(0,0,1;0.785398rad)
  Width = 6
FEATURE [Part::Box] Box159  label="Krychle159"
  AttacherType = Attacher::AttachEngine3D
  Height = 2
  Length = 8
  Placement = pos=(3,46,23) rot=(0,0,1;1.5708rad)
  Width = 6
FEATURE [Part::Box] Box160  label="Krychle160"
  AttacherType = Attacher::AttachEngine3D
  Height = 2
  Length = 8
  Placement = pos=(-30.4056,34.6482,23) rot=(0,0,1;2.35619rad)
  Width = 6
FEATURE [Part::Box] Box161  label="Krychle161"
  AttacherType = Attacher::AttachEngine3D
  Height = 2
  Length = 8
  Placement = pos=(-46,3,23) rot=(0,0,1;3.14159rad)
  Width = 6
FEATURE [Part::Box] Box162  label="Krychle162"
  AttacherType = Attacher::AttachEngine3D
  Height = 2
  Length = 8
  Placement = pos=(-34.6482,-30.4056,23) rot=(0,0,1;3.92699rad)
  Width = 6
FEATURE [Part::Box] Box163  label="Krychle163"
  AttacherType = Attacher::AttachEngine3D
  Height = 2
  Length = 8
  Placement = pos=(-3,-46,23) rot=(0,0,-1;1.5708rad)
  Width = 6
FEATURE [Part::Box] Box164  label="Krychle164"
  AttacherType = Attacher::AttachEngine3D
  Height = 2
  Length = 8
  Placement = pos=(30.4056,-34.6482,23) rot=(0,0,-1;0.785398rad)
  Width = 6
FEATURE [Part::Compound] Compound297
  Links = -> [Box157,Box158,Box159,Box160,Box161,Box162,Box163,Box164]
FEATURE [Part::Cylinder] Cylinder374  label="Válec374"
  Angle = 360
  AttacherType = Attacher::AttachEngine3D
  Height = 50
  Placement = pos=(50,0,-15) rot=(0,0,1;0rad)
  Radius = 1.5
FEATURE [Part::Cylinder] Cylinder375  label="Válec375"
  Angle = 360
  AttacherType = Attacher::AttachEngine3D
  Height = 50
  Placement = pos=(35.3553,35.3553,-15) rot=(0,0,1;0.785398rad)
  Radius = 1.5
FEATURE [Part::Cylinder] Cylinder376  label="Válec376"
  Angle = 360
  AttacherType = Attacher::AttachEngine3D
  Height = 50
  Placement = pos=(-7e-15,50,-15) rot=(0,0,1;1.5708rad)
  Radius = 1.5
FEATURE [Part::Cylinder] Cylinder377  label="Válec377"
  Angle = 360
  AttacherType = Attacher::AttachEngine3D
  Height = 50
  Placement = pos=(-35.3553,35.3553,-15) rot=(0,0,1;2.35619rad)
  Radius = 1.5
FEATURE [Part::Cylinder] Cylinder378  label="Válec378"
  Angle = 360
  AttacherType = Attacher::AttachEngine3D
  Height = 50
  Placement = pos=(-50,-2.3e-14,-15) rot=(0,0,1;3.14159rad)
  Radius = 1.5
FEATURE [Part::Cylinder] Cylinder379  label="Válec379"
  Angle = 360
  AttacherType = Attacher::AttachEngine3D
  Height = 50
  Placement = pos=(-35.3553,-35.3553,-15) rot=(0,0,1;3.92699rad)
  Radius = 1.5
FEATURE [Part::Cylinder] Cylinder380  label="Válec380"
  Angle = 360
  AttacherType = Attacher::AttachEngine3D
  Height = 50
  Placement = pos=(2.5e-14,-50,-15) rot=(0,0,-1;1.5708rad)
  Radius = 1.5
FEATURE [Part::Cylinder] Cylinder381  label="Válec381"
  Angle = 360
  AttacherType = Attacher::AttachEngine3D
  Height = 50
  Placement = pos=(35.3553,-35.3553,-15) rot=(0,0,-1;0.785398rad)
  Radius = 1.5
FEATURE [Part::Box] Box165  label="Krychle165"
  AttacherType = Attacher::AttachEngine3D
  Height = 2
  Length = 8
  Placement = pos=(3,46,23) rot=(0,0,1;1.5708rad)
  Width = 6
FEATURE [Part::Box] Box166  label="Krychle166"
  AttacherType = Attacher::AttachEngine3D
  Height = 2
  Length = 8
  Placement = pos=(-30.4056,34.6482,23) rot=(0,0,1;2.35619rad)
  Width = 6
FEATURE [Part::Cut] Cut009
  Base = -> Tube002
  Tool = -> Torus004
FEATURE [Part::Cut] Cut010
  Base = -> Cut009
  Tool = -> Cylinder006
FEATURE [Part::Cut] Cut151
  Base = -> Cut010
  Tool = -> Compound297
FEATURE [Part::Compound] Compound298
  Links = -> [Cylinder374,Cylinder375,Cylinder376,Cylinder377,Cylinder378,Cylinder379,Cylinder380,Cylinder381]
  Placement = pos=(0,0,-9) rot=(0,0,1;0rad)
FEATURE [Part::Cut] Cut152
  Base = -> Cut151
  Tool = -> Compound298
FEATURE [Part::Box] Box167  label="Krychle167"
  AttacherType = Attacher::AttachEngine3D
  Height = 2
  Length = 8
  Placement = pos=(46,-3,23) rot=(0,0,1;0rad)
  Width = 6
FEATURE [Part::Box] Box168  label="Krychle168"
  AttacherType = Attacher::AttachEngine3D
  Height = 2
  Length = 8
  Placement = pos=(-46,3,23) rot=(0,0,1;3.14159rad)
  Width = 6
FEATURE [Part::Box] Box169  label="Krychle169"
  AttacherType = Attacher::AttachEngine3D
  Height = 2
  Length = 8
  Placement = pos=(-34.6482,-30.4056,23) rot=(0,0,1;3.92699rad)
  Width = 6
FEATURE [Part::Box] Box170  label="Krychle170"
  AttacherType = Attacher::AttachEngine3D
  Height = 2
  Length = 8
  Placement = pos=(30.4056,-34.6482,23) rot=(0,0,-1;0.785398rad)
  Width = 6
FEATURE [Part::Box] Box171  label="Krychle171"
  AttacherType = Attacher::AttachEngine3D
  Height = 2
  Length = 8
  Placement = pos=(34.6482,30.4056,23) rot=(0,0,1;0.785398rad)
  Width = 6
FEATURE [Part::Box] Box172  label="Krychle172"
  AttacherType = Attacher::AttachEngine3D
  Height = 2
  Length = 8
  Placement = pos=(-3,-46,23) rot=(0,0,-1;1.5708rad)
  Width = 6
FEATURE [Part::Compound] Compound300
  Links = -> [Box167,Box171,Box165,Box166,Box168,Box169,Box172,Box170]
FEATURE [Part::Cylinder] Cylinder  label="Válec"
  Angle = 360
  AttacherType = Attacher::AttachEngine3D
  Height = 17
  Placement = pos=(0,0,20) rot=(0,0,1;0rad)
  Radius = 47
FEATURE [Part::Cut] Cut153
  Base = -> Box156
  Tool = -> Cylinder
FEATURE [Part::Cut] Cut154
  Base = -> Cut153
  Tool = -> Torus005
FEATURE [Part::Cut] Cut155
  Base = -> Cut154
  Tool = -> Compound298
FEATURE [Part::Cut] Cut156
  Base = -> Cut155
  Tool = -> Compound300
FEATURE [Part::Box] Box173  label="Krychle173"
  AttacherType = Attacher::AttachEngine3D
  Height = 6
  Length = 2
  Placement = pos=(32,48,22) rot=(0,0,1;0rad)
  Width = 6
FEATURE [Part::Cylinder] Cylinder391  label="Válec391"
  Angle = 360
  AttacherType = Attacher::AttachEngine3D
  Height = 100
  Placement = pos=(24,51,25) rot=(0,1,0;1.5708rad)
  Radius = 1.5
FEATURE [Part::Cylinder] Cylinder392  label="Válec392"
  Angle = 360
  AttacherType = Attacher::AttachEngine3D
  Height = 100
  Placement = pos=(24,-51,25) rot=(0,1,0;1.5708rad)
  Radius = 1.5
FEATURE [Part::Box] Box174  label="Krychle174"
  AttacherType = Attacher::AttachEngine3D
  Height = 6
  Length = 2
  Placement = pos=(32,-54,22) rot=(0,0,1;0rad)
  Width = 6
FEATURE [Part::Box] Box175  label="Krychle175"
  AttacherType = Attacher::AttachEngine3D
  Height = 6
  Length = 2
  Placement = pos=(38,33,31) rot=(0,0,1;0rad)
  Width = 6
FEATURE [Part::Cylinder] Cylinder393  label="Válec393"
  Angle = 360
  AttacherType = Attacher::AttachEngine3D
  Height = 100
  Placement = pos=(34,36,34) rot=(0,1,0;1.5708rad)
  Radius = 1.5
FEATURE [Part::Cylinder] Cylinder394  label="Válec394"
  Angle = 360
  AttacherType = Attacher::AttachEngine3D
  Height = 100
  Placement = pos=(34,-36,34) rot=(0,1,0;1.5708rad)
  Radius = 1.5
FEATURE [Part::Compound] Compound301
  Links = -> [Cylinder391,Cylinder392,Cylinder393,Cylinder394]
FEATURE [Part::Box] Box176  label="Krychle176"
  AttacherType = Attacher::AttachEngine3D
  Height = 6
  Length = 2
  Placement = pos=(38,-39,31) rot=(0,0,1;0rad)
  Width = 6
FEATURE [Part::Compound] Compound302
  Links = -> [Box173,Box174,Box175,Box176]
FEATURE [Part::Cylinder] Cylinder395  label="Válec395"
  Angle = 360
  AttacherType = Attacher::AttachEngine3D
  Height = 100
  Placement = pos=(34,-36,34) rot=(0,1,0;1.5708rad)
  Radius = 1.5
FEATURE [Part::Cylinder] Cylinder396  label="Válec396"
  Angle = 360
  AttacherType = Attacher::AttachEngine3D
  Height = 100
  Placement = pos=(24,51,25) rot=(0,1,0;1.5708rad)
  Radius = 1.5
FEATURE [Part::Cylinder] Cylinder397  label="Válec397"
  Angle = 360
  AttacherType = Attacher::AttachEngine3D
  Height = 100
  Placement = pos=(24,-51,25) rot=(0,1,0;1.5708rad)
  Radius = 1.5
FEATURE [Part::Cylinder] Cylinder398  label="Válec398"
  Angle = 360
  AttacherType = Attacher::AttachEngine3D
  Height = 100
  Placement = pos=(34,36,34) rot=(0,1,0;1.5708rad)
  Radius = 1.5
FEATURE [Part::Compound] Compound303
  Links = -> [Cylinder396,Cylinder397,Cylinder398,Cylinder395]
FEATURE [Part::Box] Box177  label="Krychle177"
  AttacherType = Attacher::AttachEngine3D
  Height = 6
  Length = 2
  Placement = pos=(32,48,22) rot=(0,0,1;0rad)
  Width = 6
FEATURE [Part::Box] Box178  label="Krychle178"
  AttacherType = Attacher::AttachEngine3D
  Height = 6
  Length = 2
  Placement = pos=(32,-54,22) rot=(0,0,1;0rad)
  Width = 6
FEATURE [Part::Box] Box179  label="Krychle179"
  AttacherType = Attacher::AttachEngine3D
  Height = 6
  Length = 2
  Placement = pos=(38,33,31) rot=(0,0,1;0rad)
  Width = 6
FEATURE [Part::Box] Box180  label="Krychle180"
  AttacherType = Attacher::AttachEngine3D
  Height = 6
  Length = 2
  Placement = pos=(38,-39,31) rot=(0,0,1;0rad)
  Width = 6
FEATURE [Part::Compound] Compound304
  Links = -> [Box177,Box178,Box179,Box180]
FEATURE [Part::Cut] Cut157
  Base = -> Cut156
  Tool = -> Compound301
FEATURE [Part::Cut] Cut158
  Base = -> Cut157
  Tool = -> Compound304
FEATURE [Part::Cut] Cut159
  Base = -> Cut152
  Tool = -> Compound303
FEATURE [Part::Cut] Cut160
  Base = -> Cut159
  Tool = -> Compound302
FEATURE [Part::Compound] Compound305  label="J-midi_outer-ring"
  Links = -> [Cut158,Cut160]
FEATURE [Part::Cylinder] Cylinder399  label="Válec399"
  Angle = 360
  AttacherType = Attacher::AttachEngine3D
  Height = 100
  Placement = pos=(24,51,25) rot=(0,1,0;1.5708rad)
  Radius = 1.5
FEATURE [Part::Cylinder] Cylinder400  label="Válec400"
  Angle = 360
  AttacherType = Attacher::AttachEngine3D
  Height = 100
  Placement = pos=(24,-51,25) rot=(0,1,0;1.5708rad)
  Radius = 1.5
FEATURE [Part::Cylinder] Cylinder401  label="Válec401"
  Angle = 360
  AttacherType = Attacher::AttachEngine3D
  Height = 100
  Placement = pos=(24,36,34) rot=(0,1,0;1.5708rad)
  Radius = 1.5
FEATURE [Part::Cylinder] Cylinder402  label="Válec402"
  Angle = 360
  AttacherType = Attacher::AttachEngine3D
  Height = 100
  Placement = pos=(24,-36,34) rot=(0,1,0;1.5708rad)
  Radius = 1.5
FEATURE [Part::Cylinder] Cylinder403  label="Válec403"
  Angle = 360
  AttacherType = Attacher::AttachEngine3D
  Height = 100
  Placement = pos=(24,-23,-5) rot=(0,1,0;1.5708rad)
  Radius = 1.5
FEATURE [Part::Cylinder] Cylinder404  label="Válec404"
  Angle = 360
  AttacherType = Attacher::AttachEngine3D
  Height = 100
  Placement = pos=(24,51,7) rot=(0,1,0;1.5708rad)
  Radius = 1.5
FEATURE [Part::Cylinder] Cylinder405  label="Válec405"
  Angle = 360
  AttacherType = Attacher::AttachEngine3D
  Height = 100
  Placement = pos=(24,23,-5) rot=(0,1,0;1.5708rad)
  Radius = 1.5
FEATURE [Part::Cylinder] Cylinder406  label="Válec406"
  Angle = 360
  AttacherType = Attacher::AttachEngine3D
  Height = 100
  Placement = pos=(24,-51,7) rot=(0,1,0;1.5708rad)
  Radius = 1.5
FEATURE [Part::Compound] Compound584
  Links = -> [Cylinder399,Cylinder400,Cylinder401,Cylinder402,Cylinder403,Cylinder404,Cylinder405,Cylinder406]
FEATURE [Part::Box] Box181  label="Krychle181"
  AttacherType = Attacher::AttachEngine3D
  Height = 20
  Length = 10
  Placement = pos=(97,-29,7) rot=(0,0,1;0rad)
  Width = 108
FEATURE [Part::Box] Box182  label="Krychle182"
  AttacherType = Attacher::AttachEngine3D
  Height = 2
  Length = 16
  Placement = pos=(60,2,10) rot=(0,0,1;0rad)
  Width = 6
FEATURE [Part::Box] Box183  label="Krychle183"
  AttacherType = Attacher::AttachEngine3D
  Height = 2
  Length = 16
  Placement = pos=(60,2,16) rot=(0,0,1;0rad)
  Width = 6
FEATURE [Part::Box] Box184  label="Krychle184"
  AttacherType = Attacher::AttachEngine3D
  Height = 2
  Length = 16
  Placement = pos=(60,-21,10) rot=(0,0,1;0rad)
  Width = 6
FEATURE [Part::Box] Box185  label="Krychle185"
  AttacherType = Attacher::AttachEngine3D
  Height = 2
  Length = 16
  Placement = pos=(60,-21,16) rot=(0,0,1;0rad)
  Width = 6
FEATURE [Part::Box] Box186  label="Krychle186"
  AttacherType = Attacher::AttachEngine3D
  Height = 2
  Length = 16
  Placement = pos=(60,-41,10) rot=(0,0,1;0rad)
  Width = 6
FEATURE [Part::Box] Box187  label="Krychle187"
  AttacherType = Attacher::AttachEngine3D
  Height = 2
  Length = 16
  Placement = pos=(60,-41,16) rot=(0,0,1;0rad)
  Width = 6
FEATURE [Part::Box] Box188  label="Krychle188"
  AttacherType = Attacher::AttachEngine3D
  Height = 2
  Length = 16
  Placement = pos=(60,-51,10) rot=(0,0,1;0rad)
  Width = 6
FEATURE [Part::Box] Box189  label="Krychle189"
  AttacherType = Attacher::AttachEngine3D
  Height = 2
  Length = 16
  Placement = pos=(60,-51,16) rot=(0,0,1;0rad)
  Width = 6
FEATURE [Part::Box] Box190  label="Krychle190"
  AttacherType = Attacher::AttachEngine3D
  Height = 2
  Length = 16
  Placement = pos=(60,15,10) rot=(0,0,1;0rad)
  Width = 6
FEATURE [Part::Box] Box191  label="Krychle191"
  AttacherType = Attacher::AttachEngine3D
  Height = 2
  Length = 16
  Placement = pos=(60,30,10) rot=(0,0,1;0rad)
  Width = 6
FEATURE [Part::Box] Box192  label="Krychle192"
  AttacherType = Attacher::AttachEngine3D
  Height = 2
  Length = 16
  Placement = pos=(60,46,10) rot=(0,0,1;0rad)
  Width = 6
FEATURE [Part::Box] Box193  label="Krychle193"
  AttacherType = Attacher::AttachEngine3D
  Height = 2
  Length = 16
  Placement = pos=(60,15,16) rot=(0,0,1;0rad)
  Width = 6
FEATURE [Part::Box] Box194  label="Krychle194"
  AttacherType = Attacher::AttachEngine3D
  Height = 2
  Length = 16
  Placement = pos=(60,30,16) rot=(0,0,1;0rad)
  Width = 6
FEATURE [Part::Box] Box195  label="Krychle195"
  AttacherType = Attacher::AttachEngine3D
  Height = 2
  Length = 16
  Placement = pos=(60,46,16) rot=(0,0,1;0rad)
  Width = 6
FEATURE [Part::Compound] Compound585
  Links = -> [Box182,Box183,Box184,Box185,Box186,Box187,Box188,Box189,Box190,Box191,Box192,Box193,Box194,Box195]
  Placement = pos=(39,24,3) rot=(0,0,1;0rad)
FEATURE [Part::Chamfer] Chamfer
  Base = -> Box134
  Edges = 1 edges r=5: [Edge2]
FEATURE [Part::Cylinder] Cylinder407  label="Válec407"
  Angle = 360
  AttacherType = Attacher::AttachEngine3D
  Height = 100
  Placement = pos=(24,51,25) rot=(0,1,0;1.5708rad)
  Radius = 5
FEATURE [Part::Cylinder] Cylinder408  label="Válec408"
  Angle = 360
  AttacherType = Attacher::AttachEngine3D
  Height = 100
  Placement = pos=(24,-51,25) rot=(0,1,0;1.5708rad)
  Radius = 5
FEATURE [Part::Cylinder] Cylinder409  label="Válec409"
  Angle = 360
  AttacherType = Attacher::AttachEngine3D
  Height = 100
  Placement = pos=(24,36,34) rot=(0,1,0;1.5708rad)
  Radius = 5
FEATURE [Part::Cylinder] Cylinder410  label="Válec410"
  Angle = 360
  AttacherType = Attacher::AttachEngine3D
  Height = 100
  Placement = pos=(24,-36,34) rot=(0,1,0;1.5708rad)
  Radius = 5
FEATURE [Part::Cylinder] Cylinder411  label="Válec411"
  Angle = 360
  AttacherType = Attacher::AttachEngine3D
  Height = 100
  Placement = pos=(24,-23,-5) rot=(0,1,0;1.5708rad)
  Radius = 5
FEATURE [Part::Cylinder] Cylinder412  label="Válec412"
  Angle = 360
  AttacherType = Attacher::AttachEngine3D
  Height = 100
  Placement = pos=(24,51,7) rot=(0,1,0;1.5708rad)
  Radius = 5
FEATURE [Part::Cylinder] Cylinder413  label="Válec413"
  Angle = 360
  AttacherType = Attacher::AttachEngine3D
  Height = 100
  Placement = pos=(24,23,-5) rot=(0,1,0;1.5708rad)
  Radius = 5
FEATURE [Part::Cylinder] Cylinder414  label="Válec414"
  Angle = 360
  AttacherType = Attacher::AttachEngine3D
  Height = 100
  Placement = pos=(24,-51,7) rot=(0,1,0;1.5708rad)
  Radius = 5
FEATURE [Part::Compound] Compound586
  Links = -> [Cylinder407,Cylinder408,Cylinder409,Cylinder410,Cylinder411,Cylinder412,Cylinder413,Cylinder414]
  Placement = pos=(32,0,0) rot=(0,0,1;0rad)
FEATURE [Part::Cylinder] Cylinder415  label="Válec415"
  Angle = 360
  AttacherType = Attacher::AttachEngine3D
  Height = 100
  Placement = pos=(24,51,25) rot=(0,1,0;1.5708rad)
  Radius = 5
FEATURE [Part::Cylinder] Cylinder416  label="Válec416"
  Angle = 360
  AttacherType = Attacher::AttachEngine3D
  Height = 100
  Placement = pos=(24,-51,25) rot=(0,1,0;1.5708rad)
  Radius = 5
FEATURE [Part::Cylinder] Cylinder417  label="Válec417"
  Angle = 360
  AttacherType = Attacher::AttachEngine3D
  Height = 100
  Placement = pos=(24,36,34) rot=(0,1,0;1.5708rad)
  Radius = 5
FEATURE [Part::Cylinder] Cylinder418  label="Válec418"
  Angle = 360
  AttacherType = Attacher::AttachEngine3D
  Height = 100
  Placement = pos=(24,-36,34) rot=(0,1,0;1.5708rad)
  Radius = 5
FEATURE [Part::Cylinder] Cylinder419  label="Válec419"
  Angle = 360
  AttacherType = Attacher::AttachEngine3D
  Height = 100
  Placement = pos=(24,-23,-5) rot=(0,1,0;1.5708rad)
  Radius = 5
FEATURE [Part::Cylinder] Cylinder420  label="Válec420"
  Angle = 360
  AttacherType = Attacher::AttachEngine3D
  Height = 100
  Placement = pos=(24,51,7) rot=(0,1,0;1.5708rad)
  Radius = 5
FEATURE [Part::Cylinder] Cylinder421  label="Válec421"
  Angle = 360
  AttacherType = Attacher::AttachEngine3D
  Height = 100
  Placement = pos=(24,23,-5) rot=(0,1,0;1.5708rad)
  Radius = 5
FEATURE [Part::Cylinder] Cylinder422  label="Válec422"
  Angle = 360
  AttacherType = Attacher::AttachEngine3D
  Height = 100
  Placement = pos=(24,-51,7) rot=(0,1,0;1.5708rad)
  Radius = 5
FEATURE [Part::Compound] Compound587
  Links = -> [Cylinder415,Cylinder416,Cylinder417,Cylinder418,Cylinder419,Cylinder420,Cylinder421,Cylinder422]
  Placement = pos=(32,0,0) rot=(0,0,1;0rad)
FEATURE [Part::Cut] Cut
  Base = -> Extrude
  Tool = -> Compound587
FEATURE [Part::Box] Box196  label="Krychle196"
  AttacherType = Attacher::AttachEngine3D
  Height = 45
  Length = 10
  Placement = pos=(46,-54,-8) rot=(0,0,1;0rad)
  Width = 108
FEATURE [Part::Cylinder] Cylinder423  label="Válec423"
  Angle = 360
  AttacherType = Attacher::AttachEngine3D
  Height = 100
  Placement = pos=(24,51,25) rot=(0,1,0;1.5708rad)
  Radius = 1.5
FEATURE [Part::Cylinder] Cylinder424  label="Válec424"
  Angle = 360
  AttacherType = Attacher::AttachEngine3D
  Height = 100
  Placement = pos=(24,-51,25) rot=(0,1,0;1.5708rad)
  Radius = 1.5
FEATURE [Part::Cylinder] Cylinder425  label="Válec425"
  Angle = 360
  AttacherType = Attacher::AttachEngine3D
  Height = 100
  Placement = pos=(24,36,34) rot=(0,1,0;1.5708rad)
  Radius = 1.5
FEATURE [Part::Cylinder] Cylinder426  label="Válec426"
  Angle = 360
  AttacherType = Attacher::AttachEngine3D
  Height = 100
  Placement = pos=(24,-36,34) rot=(0,1,0;1.5708rad)
  Radius = 1.5
FEATURE [Part::Cylinder] Cylinder427  label="Válec427"
  Angle = 360
  AttacherType = Attacher::AttachEngine3D
  Height = 100
  Placement = pos=(24,-23,-5) rot=(0,1,0;1.5708rad)
  Radius = 1.5
FEATURE [Part::Cylinder] Cylinder428  label="Válec428"
  Angle = 360
  AttacherType = Attacher::AttachEngine3D
  Height = 100
  Placement = pos=(24,51,7) rot=(0,1,0;1.5708rad)
  Radius = 1.5
FEATURE [Part::Cylinder] Cylinder429  label="Válec429"
  Angle = 360
  AttacherType = Attacher::AttachEngine3D
  Height = 100
  Placement = pos=(24,23,-5) rot=(0,1,0;1.5708rad)
  Radius = 1.5
FEATURE [Part::Cylinder] Cylinder430  label="Válec430"
  Angle = 360
  AttacherType = Attacher::AttachEngine3D
  Height = 100
  Placement = pos=(24,-51,7) rot=(0,1,0;1.5708rad)
  Radius = 1.5
FEATURE [Part::Compound] Compound588
  Links = -> [Cylinder423,Cylinder424,Cylinder425,Cylinder426,Cylinder427,Cylinder428,Cylinder429,Cylinder430]
FEATURE [Part::Cut] Cut361
  Base = -> Box196
  Tool = -> Compound588
FEATURE [Part::Cut] Cut362
  Base = -> Chamfer
  Tool = -> Compound586
FEATURE [Part::Cylinder] Cylinder431  label="Válec431"
  Angle = 360
  AttacherType = Attacher::AttachEngine3D
  Height = 100
  Placement = pos=(24,51,25) rot=(0,1,0;1.5708rad)
  Radius = 5
FEATURE [Part::Cylinder] Cylinder432  label="Válec432"
  Angle = 360
  AttacherType = Attacher::AttachEngine3D
  Height = 100
  Placement = pos=(24,-51,25) rot=(0,1,0;1.5708rad)
  Radius = 5
FEATURE [Part::Cylinder] Cylinder433  label="Válec433"
  Angle = 360
  AttacherType = Attacher::AttachEngine3D
  Height = 100
  Placement = pos=(24,36,34) rot=(0,1,0;1.5708rad)
  Radius = 5
FEATURE [Part::Cylinder] Cylinder434  label="Válec434"
  Angle = 360
  AttacherType = Attacher::AttachEngine3D
  Height = 100
  Placement = pos=(24,-36,34) rot=(0,1,0;1.5708rad)
  Radius = 5
FEATURE [Part::Cylinder] Cylinder435  label="Válec435"
  Angle = 360
  AttacherType = Attacher::AttachEngine3D
  Height = 100
  Placement = pos=(24,-23,-5) rot=(0,1,0;1.5708rad)
  Radius = 5
FEATURE [Part::Cylinder] Cylinder436  label="Válec436"
  Angle = 360
  AttacherType = Attacher::AttachEngine3D
  Height = 100
  Placement = pos=(24,51,7) rot=(0,1,0;1.5708rad)
  Radius = 5
FEATURE [Part::Cylinder] Cylinder437  label="Válec437"
  Angle = 360
  AttacherType = Attacher::AttachEngine3D
  Height = 100
  Placement = pos=(24,23,-5) rot=(0,1,0;1.5708rad)
  Radius = 5
FEATURE [Part::Cylinder] Cylinder438  label="Válec438"
  Angle = 360
  AttacherType = Attacher::AttachEngine3D
  Height = 100
  Placement = pos=(24,-51,7) rot=(0,1,0;1.5708rad)
  Radius = 5
FEATURE [Part::Compound] Compound589
  Links = -> [Cylinder431,Cylinder432,Cylinder433,Cylinder434,Cylinder435,Cylinder436,Cylinder437,Cylinder438]
  Placement = pos=(32,0,0) rot=(0,0,1;0rad)
FEATURE [Part::Cut] Cut363
  Base = -> Box181
  Tool = -> Compound589
FEATURE [Part::Cylinder] Cylinder439  label="Válec439"
  Angle = 360
  AttacherType = Attacher::AttachEngine3D
  Height = 50
  Placement = pos=(63,5,-12) rot=(0,0,1;0rad)
  Radius = 1.5
FEATURE [Part::Cylinder] Cylinder440  label="Válec440"
  Angle = 360
  AttacherType = Attacher::AttachEngine3D
  Height = 50
  Placement = pos=(63,-18,-12) rot=(0,0,1;0rad)
  Radius = 1.5
FEATURE [Part::Cylinder] Cylinder441  label="Válec441"
  Angle = 360
  AttacherType = Attacher::AttachEngine3D
  Height = 50
  Placement = pos=(63,-38,-12) rot=(0,0,1;0rad)
  Radius = 1.5
FEATURE [Part::Cylinder] Cylinder442  label="Válec442"
  Angle = 360
  AttacherType = Attacher::AttachEngine3D
  Height = 50
  Placement = pos=(63,-48,-12) rot=(0,0,1;0rad)
  Radius = 1.5
FEATURE [Part::Cylinder] Cylinder443  label="Válec443"
  Angle = 360
  AttacherType = Attacher::AttachEngine3D
  Height = 50
  Placement = pos=(63,18,-12) rot=(0,0,1;0rad)
  Radius = 1.5
FEATURE [Part::Cylinder] Cylinder444  label="Válec444"
  Angle = 360
  AttacherType = Attacher::AttachEngine3D
  Height = 50
  Placement = pos=(63,33,-12) rot=(0,0,1;0rad)
  Radius = 1.5
FEATURE [Part::Cylinder] Cylinder445  label="Válec445"
  Angle = 360
  AttacherType = Attacher::AttachEngine3D
  Height = 50
  Placement = pos=(63,49,-12) rot=(0,0,1;0rad)
  Radius = 1.5
FEATURE [Part::Compound] Compound590
  Links = -> [Cylinder439,Cylinder440,Cylinder441,Cylinder442,Cylinder443,Cylinder444,Cylinder445]
  Placement = pos=(39,24,0) rot=(0,0,1;0rad)
FEATURE [Part::Cut] Cut364
  Base = -> Cut363
  Tool = -> Compound590
FEATURE [Part::Cut] Cut365
  Base = -> Cut364
  Tool = -> Compound585
FEATURE [Part::Cylinder] Cylinder446  label="Válec446"
  Angle = 360
  AttacherType = Attacher::AttachEngine3D
  Height = 28
  Placement = pos=(0,0,9) rot=(0,0,1;0rad)
  Radius = 54.5
FEATURE [Part::Cut] Cut366
  Base = -> Cut361
  Tool = -> Cylinder446
FEATURE [Part::Cylinder] Cylinder447  label="Válec447"
  Angle = 360
  AttacherType = Attacher::AttachEngine3D
  Height = 4
  Placement = pos=(50,0,5) rot=(0,0,1;0rad)
  Radius = 3.5
FEATURE [Part::Cut] Cut367
  Base = -> Cut366
  Tool = -> Cylinder447
FEATURE [Part::Compound] Compound591  label="G-midi_adaptor-subshifted"
  Links = -> [Cut,Cut362,Cut365,Cut367]
FEATURE [Sketcher::SketchObject] Sketch001
  FullyConstrained = true
  Placement = pos=(0,-54,-8) rot=(0.57735,0.57735,0.57735;2.0944rad)
  sketch-geometry (4):
    g0: LineSegment StartX=0 StartY=0 StartZ=0 EndX=108 EndY=0 EndZ=0
    g1: LineSegment StartX=108 StartY=0 StartZ=0 EndX=108 EndY=45 EndZ=0
    g2: LineSegment StartX=108 StartY=45 StartZ=0 EndX=0 EndY=45 EndZ=0
    g3: LineSegment StartX=0 StartY=45 StartZ=0 EndX=0 EndY=0 EndZ=0
  constraints (11):
    c: Coincident(g0,g1)
    c: Coincident(g1,g2)
    c: Coincident(g2,g3)
    c: Coincident(g3,g0)
    c: Horizontal(g0)
    c: Horizontal(g2)
    c: Vertical(g1)
    c: Vertical(g3)
    c: Distance(g1) = 45
    c: Distance(g2) = 108
    c: Coincident(g-1,g0)
FEATURE [Part::Extrusion] Extrude001
  Base = -> Sketch001
  Dir = (1,0.8,0)
  DirMode = 0
  FaceMakerClass = Part::FaceMakerBullseye
  LengthFwd = 50
  LengthRev = 0
  Placement = pos=(56,0,0) rot=(0,0,1;0rad)
  Solid = true
  Symmetric = false
FEATURE [Part::Box] Box197  label="Krychle197"
  AttacherType = Attacher::AttachEngine3D
  Height = 50
  Length = 10
  Placement = pos=(87,-29,-8) rot=(0,0,1;0rad)
  Width = 108
FEATURE [Part::Box] Box198  label="Krychle198"
  AttacherType = Attacher::AttachEngine3D
  Height = 2
  Length = 16
  Placement = pos=(60,-41,16) rot=(0,0,1;0rad)
  Width = 6
FEATURE [Part::Box] Box201  label="Krychle201"
  AttacherType = Attacher::AttachEngine3D
  Height = 20
  Length = 10
  Placement = pos=(97,-29,7) rot=(0,0,1;0rad)
  Width = 108
FEATURE [Part::Box] Box202  label="Krychle202"
  AttacherType = Attacher::AttachEngine3D
  Height = 2
  Length = 16
  Placement = pos=(60,2,16) rot=(0,0,1;0rad)
  Width = 6
FEATURE [Part::Box] Box204  label="Krychle204"
  AttacherType = Attacher::AttachEngine3D
  Height = 2
  Length = 16
  Placement = pos=(60,-41,10) rot=(0,0,1;0rad)
  Width = 6
FEATURE [Part::Box] Box205  label="Krychle205"
  AttacherType = Attacher::AttachEngine3D
  Height = 2
  Length = 16
  Placement = pos=(60,-51,16) rot=(0,0,1;0rad)
  Width = 6
FEATURE [Part::Box] Box209  label="Krychle209"
  AttacherType = Attacher::AttachEngine3D
  Height = 2
  Length = 16
  Placement = pos=(60,-51,10) rot=(0,0,1;0rad)
  Width = 6
FEATURE [Part::Box] Box211  label="Krychle211"
  AttacherType = Attacher::AttachEngine3D
  Height = 2
  Length = 16
  Placement = pos=(60,46,16) rot=(0,0,1;0rad)
  Width = 6
FEATURE [Part::Cylinder] Cylinder448  label="Válec448"
  Angle = 360
  AttacherType = Attacher::AttachEngine3D
  Height = 100
  Placement = pos=(24,51,25) rot=(0,1,0;1.5708rad)
  Radius = 5
FEATURE [Part::Cylinder] Cylinder449  label="Válec449"
  Angle = 360
  AttacherType = Attacher::AttachEngine3D
  Height = 100
  Placement = pos=(24,36,34) rot=(0,1,0;1.5708rad)
  Radius = 5
FEATURE [Part::Cylinder] Cylinder450  label="Válec450"
  Angle = 360
  AttacherType = Attacher::AttachEngine3D
  Height = 100
  Placement = pos=(24,51,7) rot=(0,1,0;1.5708rad)
  Radius = 5
FEATURE [Part::Cylinder] Cylinder451  label="Válec451"
  Angle = 360
  AttacherType = Attacher::AttachEngine3D
  Height = 100
  Placement = pos=(24,-51,7) rot=(0,1,0;1.5708rad)
  Radius = 5
FEATURE [Part::Cylinder] Cylinder452  label="Válec452"
  Angle = 360
  AttacherType = Attacher::AttachEngine3D
  Height = 100
  Placement = pos=(24,51,25) rot=(0,1,0;1.5708rad)
  Radius = 5
FEATURE [Part::Cylinder] Cylinder453  label="Válec453"
  Angle = 360
  AttacherType = Attacher::AttachEngine3D
  Height = 100
  Placement = pos=(24,-51,25) rot=(0,1,0;1.5708rad)
  Radius = 5
FEATURE [Part::Cylinder] Cylinder454  label="Válec454"
  Angle = 360
  AttacherType = Attacher::AttachEngine3D
  Height = 100
  Placement = pos=(24,36,34) rot=(0,1,0;1.5708rad)
  Radius = 5
FEATURE [Part::Cylinder] Cylinder455  label="Válec455"
  Angle = 360
  AttacherType = Attacher::AttachEngine3D
  Height = 100
  Placement = pos=(24,-51,25) rot=(0,1,0;1.5708rad)
  Radius = 5
FEATURE [Part::Cylinder] Cylinder456  label="Válec456"
  Angle = 360
  AttacherType = Attacher::AttachEngine3D
  Height = 100
  Placement = pos=(24,-23,-5) rot=(0,1,0;1.5708rad)
  Radius = 5
FEATURE [Part::Cylinder] Cylinder457  label="Válec457"
  Angle = 360
  AttacherType = Attacher::AttachEngine3D
  Height = 100
  Placement = pos=(24,-36,34) rot=(0,1,0;1.5708rad)
  Radius = 5
FEATURE [Part::Cylinder] Cylinder458  label="Válec458"
  Angle = 360
  AttacherType = Attacher::AttachEngine3D
  Height = 100
  Placement = pos=(24,23,-5) rot=(0,1,0;1.5708rad)
  Radius = 5
FEATURE [Part::Cylinder] Cylinder459  label="Válec459"
  Angle = 360
  AttacherType = Attacher::AttachEngine3D
  Height = 100
  Placement = pos=(24,-36,34) rot=(0,1,0;1.5708rad)
  Radius = 5
FEATURE [Part::Compound] Compound595
  Links = -> [Cylinder448,Cylinder455,Cylinder449,Cylinder457,Cylinder456,Cylinder450,Cylinder458,Cylinder451]
  Placement = pos=(32,0,0) rot=(0,0,1;0rad)
FEATURE [Part::Chamfer] Chamfer001
  Base = -> Box197
  Edges = 1 edges r=5: [Edge2]
  Placement = pos=(8,6,0) rot=(0,0,1;0rad)
FEATURE [Part::Cut] Cut369
  Base = -> Chamfer001
  Tool = -> Compound595
FEATURE [Part::Box] Box213  label="Krychle213"
  AttacherType = Attacher::AttachEngine3D
  Height = 45
  Length = 10
  Placement = pos=(46,-54,-8) rot=(0,0,1;0rad)
  Width = 108
FEATURE [Part::Cylinder] Cylinder460  label="Válec460"
  Angle = 360
  AttacherType = Attacher::AttachEngine3D
  Height = 100
  Placement = pos=(24,51,7) rot=(0,1,0;1.5708rad)
  Radius = 1.5
FEATURE [Part::Cylinder] Cylinder461  label="Válec461"
  Angle = 360
  AttacherType = Attacher::AttachEngine3D
  Height = 100
  Placement = pos=(24,-36,34) rot=(0,1,0;1.5708rad)
  Radius = 5
FEATURE [Part::Cylinder] Cylinder462  label="Válec462"
  Angle = 360
  AttacherType = Attacher::AttachEngine3D
  Height = 100
  Placement = pos=(24,51,7) rot=(0,1,0;1.5708rad)
  Radius = 5
FEATURE [Part::Cylinder] Cylinder463  label="Válec463"
  Angle = 360
  AttacherType = Attacher::AttachEngine3D
  Height = 100
  Placement = pos=(24,23,-5) rot=(0,1,0;1.5708rad)
  Radius = 1.5
FEATURE [Part::Cylinder] Cylinder464  label="Válec464"
  Angle = 360
  AttacherType = Attacher::AttachEngine3D
  Height = 100
  Placement = pos=(24,-36,34) rot=(0,1,0;1.5708rad)
  Radius = 1.5
FEATURE [Part::Cylinder] Cylinder465  label="Válec465"
  Angle = 360
  AttacherType = Attacher::AttachEngine3D
  Height = 100
  Placement = pos=(24,23,-5) rot=(0,1,0;1.5708rad)
  Radius = 5
FEATURE [Part::Cylinder] Cylinder466  label="Válec466"
  Angle = 360
  AttacherType = Attacher::AttachEngine3D
  Height = 100
  Placement = pos=(24,-23,-5) rot=(0,1,0;1.5708rad)
  Radius = 1.5
FEATURE [Part::Cylinder] Cylinder467  label="Válec467"
  Angle = 360
  AttacherType = Attacher::AttachEngine3D
  Height = 50
  Placement = pos=(63,-38,-12) rot=(0,0,1;0rad)
  Radius = 1.5
FEATURE [Part::Cylinder] Cylinder468  label="Válec468"
  Angle = 360
  AttacherType = Attacher::AttachEngine3D
  Height = 100
  Placement = pos=(24,-51,7) rot=(0,1,0;1.5708rad)
  Radius = 1.5
FEATURE [Part::Cylinder] Cylinder469  label="Válec469"
  Angle = 360
  AttacherType = Attacher::AttachEngine3D
  Height = 100
  Placement = pos=(24,-23,-5) rot=(0,1,0;1.5708rad)
  Radius = 5
FEATURE [Part::Cylinder] Cylinder470  label="Válec470"
  Angle = 360
  AttacherType = Attacher::AttachEngine3D
  Height = 100
  Placement = pos=(24,51,25) rot=(0,1,0;1.5708rad)
  Radius = 1.5
FEATURE [Part::Cylinder] Cylinder471  label="Válec471"
  Angle = 360
  AttacherType = Attacher::AttachEngine3D
  Height = 100
  Placement = pos=(24,36,34) rot=(0,1,0;1.5708rad)
  Radius = 1.5
FEATURE [Part::Cylinder] Cylinder472  label="Válec472"
  Angle = 360
  AttacherType = Attacher::AttachEngine3D
  Height = 100
  Placement = pos=(24,-51,7) rot=(0,1,0;1.5708rad)
  Radius = 5
FEATURE [Part::Compound] Compound598
  Links = -> [Cylinder452,Cylinder453,Cylinder454,Cylinder459,Cylinder469,Cylinder462,Cylinder465,Cylinder472]
  Placement = pos=(32,0,0) rot=(0,0,1;0rad)
FEATURE [Part::Cut] Cut368
  Base = -> Extrude001
  Tool = -> Compound598
FEATURE [Part::Cylinder] Cylinder473  label="Válec473"
  Angle = 360
  AttacherType = Attacher::AttachEngine3D
  Height = 100
  Placement = pos=(24,-51,25) rot=(0,1,0;1.5708rad)
  Radius = 1.5
FEATURE [Part::Compound] Compound594
  Links = -> [Cylinder470,Cylinder473,Cylinder471,Cylinder464,Cylinder466,Cylinder460,Cylinder463,Cylinder468]
FEATURE [Part::Cut] Cut374
  Base = -> Box213
  Tool = -> Compound594
FEATURE [Part::Cylinder] Cylinder474  label="Válec474"
  Angle = 360
  AttacherType = Attacher::AttachEngine3D
  Height = 100
  Placement = pos=(24,51,25) rot=(0,1,0;1.5708rad)
  Radius = 5
FEATURE [Part::Cylinder] Cylinder475  label="Válec475"
  Angle = 360
  AttacherType = Attacher::AttachEngine3D
  Height = 100
  Placement = pos=(24,36,34) rot=(0,1,0;1.5708rad)
  Radius = 5
FEATURE [Part::Cylinder] Cylinder476  label="Válec476"
  Angle = 360
  AttacherType = Attacher::AttachEngine3D
  Height = 100
  Placement = pos=(24,-51,25) rot=(0,1,0;1.5708rad)
  Radius = 5
FEATURE [Part::Cylinder] Cylinder477  label="Válec477"
  Angle = 360
  AttacherType = Attacher::AttachEngine3D
  Height = 100
  Placement = pos=(24,-23,-5) rot=(0,1,0;1.5708rad)
  Radius = 5
FEATURE [Part::Cylinder] Cylinder478  label="Válec478"
  Angle = 360
  AttacherType = Attacher::AttachEngine3D
  Height = 100
  Placement = pos=(24,23,-5) rot=(0,1,0;1.5708rad)
  Radius = 5
FEATURE [Part::Cylinder] Cylinder479  label="Válec479"
  Angle = 360
  AttacherType = Attacher::AttachEngine3D
  Height = 100
  Placement = pos=(24,-51,7) rot=(0,1,0;1.5708rad)
  Radius = 5
FEATURE [Part::Cylinder] Cylinder480  label="Válec480"
  Angle = 360
  AttacherType = Attacher::AttachEngine3D
  Height = 50
  Placement = pos=(63,-18,-12) rot=(0,0,1;0rad)
  Radius = 1.5
FEATURE [Part::Cylinder] Cylinder481  label="Válec481"
  Angle = 360
  AttacherType = Attacher::AttachEngine3D
  Height = 100
  Placement = pos=(24,51,7) rot=(0,1,0;1.5708rad)
  Radius = 5
FEATURE [Part::Compound] Compound596
  Links = -> [Cylinder474,Cylinder476,Cylinder475,Cylinder461,Cylinder477,Cylinder481,Cylinder478,Cylinder479]
  Placement = pos=(24,-6,0) rot=(0,0,1;0rad)
FEATURE [Part::Cut] Cut370
  Base = -> Box201
  Tool = -> Compound596
FEATURE [Part::Cylinder] Cylinder482  label="Válec482"
  Angle = 360
  AttacherType = Attacher::AttachEngine3D
  Height = 50
  Placement = pos=(63,5,-12) rot=(0,0,1;0rad)
  Radius = 1.5
FEATURE [Part::Cylinder] Cylinder483  label="Válec483"
  Angle = 360
  AttacherType = Attacher::AttachEngine3D
  Height = 50
  Placement = pos=(63,-48,-12) rot=(0,0,1;0rad)
  Radius = 1.5
FEATURE [Part::Cylinder] Cylinder484  label="Válec484"
  Angle = 360
  AttacherType = Attacher::AttachEngine3D
  Height = 28
  Placement = pos=(0,0,9) rot=(0,0,1;0rad)
  Radius = 54.5
FEATURE [Part::Cut] Cut375
  Base = -> Cut374
  Tool = -> Cylinder484
FEATURE [Part::Cylinder] Cylinder485  label="Válec485"
  Angle = 360
  AttacherType = Attacher::AttachEngine3D
  Height = 4
  Placement = pos=(50,0,5) rot=(0,0,1;0rad)
  Radius = 3.5
FEATURE [Part::Cut] Cut371
  Base = -> Cut375
  Tool = -> Cylinder485
FEATURE [Part::Cylinder] Cylinder486  label="Válec486"
  Angle = 360
  AttacherType = Attacher::AttachEngine3D
  Height = 50
  Placement = pos=(63,33,-12) rot=(0,0,1;0rad)
  Radius = 1.5
FEATURE [Part::Cylinder] Cylinder488  label="Válec488"
  Angle = 360
  AttacherType = Attacher::AttachEngine3D
  Height = 50
  Placement = pos=(63,49,-12) rot=(0,0,1;0rad)
  Radius = 1.5
FEATURE [Part::Compound] Compound593
  Links = -> [Cylinder482,Cylinder480,Cylinder467,Cylinder483,Cylinder486,Cylinder488]
  Placement = pos=(39,24,0) rot=(0,0,1;0rad)
FEATURE [Part::Cut] Cut372
  Base = -> Cut370
  Tool = -> Compound593
FEATURE [Part::Box] Box206  label="Krychle206"
  AttacherType = Attacher::AttachEngine3D
  Height = 2
  Length = 16
  Placement = pos=(60,-21,16) rot=(0,0,1;0rad)
  Width = 6
FEATURE [Part::Box] Box200  label="Krychle200"
  AttacherType = Attacher::AttachEngine3D
  Height = 2
  Length = 16
  Placement = pos=(60,46,10) rot=(0,0,1;0rad)
  Width = 6
FEATURE [Part::Box] Box208  label="Krychle208"
  AttacherType = Attacher::AttachEngine3D
  Height = 2
  Length = 16
  Placement = pos=(60,-21,10) rot=(0,0,1;0rad)
  Width = 6
FEATURE [Part::Box] Box203  label="Krychle203"
  AttacherType = Attacher::AttachEngine3D
  Height = 2
  Length = 16
  Placement = pos=(60,2,10) rot=(0,0,1;0rad)
  Width = 6
FEATURE [Part::Box] Box207  label="Krychle207"
  AttacherType = Attacher::AttachEngine3D
  Height = 2
  Length = 16
  Placement = pos=(60,30,10) rot=(0,0,1;0rad)
  Width = 6
FEATURE [Part::Box] Box212  label="Krychle212"
  AttacherType = Attacher::AttachEngine3D
  Height = 2
  Length = 16
  Placement = pos=(60,30,16) rot=(0,0,1;0rad)
  Width = 6
FEATURE [Part::Compound] Compound592
  Links = -> [Box203,Box202,Box208,Box206,Box204,Box198,Box209,Box205,Box207,Box200,Box212,Box211]
  Placement = pos=(39,24,3) rot=(0,0,1;0rad)
FEATURE [Part::Cut] Cut373
  Base = -> Cut372
  Placement = pos=(8,6,0) rot=(0,0,1;0rad)
  Tool = -> Compound592
FEATURE [Part::Compound] Compound597  label="G-midi_adaptor-supershifted"
  Links = -> [Cut368,Cut369,Cut373,Cut371]
FEATURE [Mesh::Feature] Mesh  label="G-midi_adaptor-supershifted (Meshed)"
FEATURE [Part::FeaturePython] Tube086  # WARN: FeaturePython — macro-defined, semantics opaque (R4)
  AttacherType = Attacher::AttachEngine3D
  Height = 16
  InnerRadius = 29.1
  OuterRadius = 35
FEATURE [Part::FeaturePython] Tube088  # WARN: FeaturePython — macro-defined, semantics opaque (R4)
  AttacherType = Attacher::AttachEngine3D
  Height = 3
  InnerRadius = 26
  OuterRadius = 35
  Placement = pos=(0,0,-3) rot=(0,0,1;0rad)
FEATURE [Part::Box] Box688  label="Krychle688"
  AttacherType = Attacher::AttachEngine3D
  Height = 50
  Length = 42
  Placement = pos=(-21,58,38) rot=(0,0,1;0rad)
  Width = 64
FEATURE [Part::Cylinder] Cylinder1734  label="Válec1734"
  Angle = 360
  AttacherType = Attacher::AttachEngine3D
  Height = 60
  Placement = pos=(15,125,-80) rot=(0,0,1;0rad)
  Radius = 1.5
FEATURE [Part::Box] Box686  label="Krychle686"
  AttacherType = Attacher::AttachEngine3D
  Height = 10
  Length = 54
  Placement = pos=(-27.0044,59.998,75) rot=(0,0,1;0rad)
  Width = 68
FEATURE [Part::Cut] Cut500
  Base = -> Box686
  Tool = -> Box688
FEATURE [Part::Box] Box690  label="Krychle690"
  AttacherType = Attacher::AttachEngine3D
  Height = 2
  Length = 6
  Placement = pos=(-18,122,-48) rot=(0,0,1;0rad)
  Width = 6
FEATURE [Part::Box] Box691  label="Krychle691"
  AttacherType = Attacher::AttachEngine3D
  Height = 2
  Length = 6
  Placement = pos=(21,70,-48) rot=(0,0,1;0rad)
  Width = 6
FEATURE [Part::Box] Box689  label="Krychle689"
  AttacherType = Attacher::AttachEngine3D
  Height = 2
  Length = 7
  Placement = pos=(-28,70,-48) rot=(0,0,1;0rad)
  Width = 6
FEATURE [Part::Cylinder] Cylinder1730  label="Válec1730"
  Angle = 360
  AttacherType = Attacher::AttachEngine3D
  Height = 50
  Placement = pos=(24,140,72) rot=(1,0,0;1.5708rad)
  Radius = 1.5
FEATURE [Part::Cylinder] Cylinder1731  label="Válec1731"
  Angle = 360
  AttacherType = Attacher::AttachEngine3D
  Height = 60
  Placement = pos=(24,73,-80) rot=(0,0,1;0rad)
  Radius = 1.5
FEATURE [Part::Cylinder] Cylinder1732  label="Válec1732"
  Angle = 360
  AttacherType = Attacher::AttachEngine3D
  Height = 60
  Placement = pos=(-24,73,-80) rot=(0,0,1;0rad)
  Radius = 1.5
FEATURE [Part::Cylinder] Cylinder1733  label="Válec1733"
  Angle = 360
  AttacherType = Attacher::AttachEngine3D
  Height = 60
  Placement = pos=(-15,125,-80) rot=(0,0,1;0rad)
  Radius = 1.5
FEATURE [Part::Compound] Compound874
  Links = -> [Cylinder1731,Cylinder1732,Cylinder1733,Cylinder1734]
  Placement = pos=(0,0,120) rot=(0,0,1;0rad)
FEATURE [Part::Cylinder] Cylinder1727  label="Válec1727"
  Angle = 360
  AttacherType = Attacher::AttachEngine3D
  Height = 3
  Placement = pos=(-24,128,72) rot=(1,0,0;1.5708rad)
  Radius = 3
FEATURE [Part::Cylinder] Cylinder1728  label="Válec1728"
  Angle = 360
  AttacherType = Attacher::AttachEngine3D
  Height = 3
  Placement = pos=(24,128,72) rot=(1,0,0;1.5708rad)
  Radius = 3
FEATURE [Part::Compound] Compound871
  Links = -> [Cylinder1727,Cylinder1728]
  Placement = pos=(0,0,8) rot=(0,0,1;0rad)
FEATURE [Part::Cylinder] Cylinder1729  label="Válec1729"
  Angle = 360
  AttacherType = Attacher::AttachEngine3D
  Height = 50
  Placement = pos=(-24,140,72) rot=(1,0,0;1.5708rad)
  Radius = 1.5
FEATURE [Part::Compound] Compound873
  Links = -> [Cylinder1729,Cylinder1730]
  Placement = pos=(0,0,8) rot=(0,0,1;0rad)
FEATURE [Part::Box] Box692  label="Krychle692"
  AttacherType = Attacher::AttachEngine3D
  Height = 2
  Length = 6
  Placement = pos=(12,122,-48) rot=(0,0,1;0rad)
  Width = 6
FEATURE [Part::Compound] Compound872
  Links = -> [Box689,Box690,Box691,Box692]
  Placement = pos=(0,0,127) rot=(0,0,1;0rad)
FEATURE [Part::Box] Box693  label="Krychle693"
  AttacherType = Attacher::AttachEngine3D
  Height = 10
  Length = 56
  Placement = pos=(-28,78,75) rot=(0,0,1;0rad)
  Width = 44
FEATURE [Part::Cut] Cut501
  Base = -> Cut500
  Tool = -> Box693
FEATURE [Part::Box] Box695  label="Krychle695"
  AttacherType = Attacher::AttachEngine3D
  Height = 50
  Length = 42
  Placement = pos=(-21,58,40) rot=(0,0,1;0rad)
  Width = 64
FEATURE [Part::Cylinder] Cylinder1738  label="Válec1738"
  Angle = 360
  AttacherType = Attacher::AttachEngine3D
  Height = 60
  Placement = pos=(-15,125,-80) rot=(0,0,1;0rad)
  Radius = 1.5
FEATURE [Part::Cylinder] Cylinder1735  label="Válec1735"
  Angle = 360
  AttacherType = Attacher::AttachEngine3D
  Height = 60
  Placement = pos=(15,125,-80) rot=(0,0,1;0rad)
  Radius = 1.5
FEATURE [Part::Cylinder] Cylinder1736  label="Válec1736"
  Angle = 360
  AttacherType = Attacher::AttachEngine3D
  Height = 60
  Placement = pos=(24,73,-80) rot=(0,0,1;0rad)
  Radius = 1.5
FEATURE [Part::Cylinder] Cylinder1737  label="Válec1737"
  Angle = 360
  AttacherType = Attacher::AttachEngine3D
  Height = 60
  Placement = pos=(-24,73,-80) rot=(0,0,1;0rad)
  Radius = 1.5
FEATURE [Part::Compound] Compound875
  Links = -> [Cylinder1736,Cylinder1737,Cylinder1738,Cylinder1735]
  Placement = pos=(0,0,120) rot=(0,0,1;0rad)
FEATURE [Part::Cut] Cut503
  Base = -> Cut501
  Tool = -> Compound875
FEATURE [Part::Cut] Cut504
  Base = -> Cut503
  Tool = -> Compound872
FEATURE [Part::Chamfer] Chamfer054
  Base = -> Cut504
  Edges = 2 edges r=3: [Edge32,Edge43]
FEATURE [Part::Cut] Cut505
  Base = -> Chamfer054
  Tool = -> Compound871
FEATURE [Part::Cut] Cut506
  Base = -> Cut505
  Tool = -> Compound873
FEATURE [Part::Box] Box694  label="Krychle694"
  AttacherType = Attacher::AttachEngine3D
  Height = 9
  Length = 54
  Placement = pos=(-27.0044,59.998,75) rot=(0,0,1;0rad)
  Width = 68
FEATURE [Part::Cut] Cut502
  Base = -> Box694
  Placement = pos=(0,0,-9) rot=(0,0,1;0rad)
  Tool = -> Box695
FEATURE [Part::Chamfer] Chamfer055
  Base = -> Cut502
  Edges = 2 edges r=3: [Edge3,Edge15]
FEATURE [Part::Cut] Cut507
  Base = -> Chamfer055
  Tool = -> Compound874
FEATURE [Part::Compound] Compound876
  Links = -> [Cut506,Cut507]
  Placement = pos=(-39,0,-69) rot=(0,0,-1;1.5708rad)
FEATURE [Part::Box] Box696  label="Krychle696"
  AttacherType = Attacher::AttachEngine3D
  Height = 2
  Length = 6
  Placement = pos=(-3,-35,6) rot=(0,0,1;0rad)
  Width = 6
FEATURE [Part::Box] Box702  label="Krychle702"
  AttacherType = Attacher::AttachEngine3D
  Height = 2
  Length = 6
  Placement = pos=(-35,3,6) rot=(0,0,-1;1.5708rad)
  Width = 6
FEATURE [Part::Box] Box699  label="Krychle699"
  AttacherType = Attacher::AttachEngine3D
  Height = 2
  Length = 6
  Placement = pos=(26.8701,22.6274,6) rot=(0,0,1;2.35619rad)
  Width = 6
FEATURE [Part::Box] Box703  label="Krychle703"
  AttacherType = Attacher::AttachEngine3D
  Height = 2
  Length = 6
  Placement = pos=(-26.8701,-22.6274,6) rot=(0,0,-1;0.785398rad)
  Width = 6
FEATURE [Part::Box] Box700  label="Krychle700"
  AttacherType = Attacher::AttachEngine3D
  Height = 2
  Length = 6
  Placement = pos=(3,35,6) rot=(0,0,1;3.14159rad)
  Width = 6
FEATURE [Part::Box] Box697  label="Krychle697"
  AttacherType = Attacher::AttachEngine3D
  Height = 2
  Length = 6
  Placement = pos=(22.6274,-26.8701,6) rot=(0,0,1;0.785398rad)
  Width = 6
FEATURE [Part::Box] Box698  label="Krychle698"
  AttacherType = Attacher::AttachEngine3D
  Height = 2
  Length = 6
  Placement = pos=(35,-3,6) rot=(0,0,1;1.5708rad)
  Width = 6
FEATURE [Part::Box] Box701  label="Krychle701"
  AttacherType = Attacher::AttachEngine3D
  Height = 2
  Length = 6
  Placement = pos=(-22.6274,26.8701,6) rot=(0,0,1;3.92699rad)
  Width = 6
FEATURE [Part::Compound] Compound878
  Links = -> [Box696,Box697,Box703,Box702,Box701,Box700,Box699,Box698]
FEATURE [Part::Cylinder] Cylinder1771  label="Válec1771"
  Angle = 360
  AttacherType = Attacher::AttachEngine3D
  Height = 30
  Placement = pos=(0,-32,0) rot=(0,0,1;0rad)
  Radius = 1.5
FEATURE [Part::Cylinder] Cylinder1766  label="Válec1766"
  Angle = 360
  AttacherType = Attacher::AttachEngine3D
  Height = 30
  Placement = pos=(-22.6274,-22.6274,0) rot=(0,0,-1;0.785398rad)
  Radius = 1.5
FEATURE [Part::Cylinder] Cylinder1764  label="Válec1764"
  Angle = 360
  AttacherType = Attacher::AttachEngine3D
  Height = 30
  Placement = pos=(22.6274,22.6274,0) rot=(0,0,1;2.35619rad)
  Radius = 1.5
FEATURE [Part::Cylinder] Cylinder1767  label="Válec1767"
  Angle = 360
  AttacherType = Attacher::AttachEngine3D
  Height = 30
  Placement = pos=(-1e-14,32,0) rot=(0,0,1;3.14159rad)
  Radius = 1.5
FEATURE [Part::Cylinder] Cylinder1768  label="Válec1768"
  Angle = 360
  AttacherType = Attacher::AttachEngine3D
  Height = 30
  Placement = pos=(32,0,0) rot=(0,0,1;1.5708rad)
  Radius = 1.5
FEATURE [Part::Cylinder] Cylinder1770  label="Válec1770"
  Angle = 360
  AttacherType = Attacher::AttachEngine3D
  Height = 30
  Placement = pos=(22.6274,-22.6274,0) rot=(0,0,1;0.785398rad)
  Radius = 1.5
FEATURE [Part::Cylinder] Cylinder1765  label="Válec1765"
  Angle = 360
  AttacherType = Attacher::AttachEngine3D
  Height = 30
  Placement = pos=(-22.6274,22.6274,0) rot=(0,0,1;3.92699rad)
  Radius = 1.5
FEATURE [Part::Cylinder] Cylinder1769  label="Válec1769"
  Angle = 360
  AttacherType = Attacher::AttachEngine3D
  Height = 30
  Placement = pos=(-32,-1.1e-14,0) rot=(0,0,-1;1.5708rad)
  Radius = 1.5
FEATURE [Part::Compound] Compound881
  Links = -> [Cylinder1771,Cylinder1770,Cylinder1768,Cylinder1764,Cylinder1767,Cylinder1765,Cylinder1769,Cylinder1766]
FEATURE [Part::Cut] Cut511
  Base = -> Tube086
  Tool = -> Compound881
FEATURE [Part::Cut] Cut512
  Base = -> Cut511
  Tool = -> Compound878
FEATURE [Part::Cylinder] Cylinder1794  label="Válec1794"
  Angle = 360
  AttacherType = Attacher::AttachEngine3D
  Height = 32
  Placement = pos=(0,0,-3) rot=(0,0,1;0rad)
  Radius = 35
FEATURE [Part::Cut] Cut526
  Base = -> Compound876
  Placement = pos=(0,0,0) rot=(0,0,1;3.14159rad)
  Tool = -> Cylinder1794
FEATURE [Part::Compound] Compound889  label="G-midi_bear-hold-encoder-rear1"
  Links = -> [Cut512,Cut526,Tube088]
  Placement = pos=(0,0,-1) rot=(0,0,1;0rad)
FEATURE [Part::Cylinder] Cylinder1795  label="Válec1795"
  Angle = 360
  AttacherType = Attacher::AttachEngine3D
  Height = 64
  Placement = pos=(-32,42,1) rot=(0,1,0;1.5708rad)
  Radius = 1.5
FEATURE [Part::Cylinder] Cylinder1798  label="Válec1798"
  Angle = 360
  AttacherType = Attacher::AttachEngine3D
  Height = 16
  Placement = pos=(-32,42,17) rot=(0,1,0;1.5708rad)
  Radius = 4
FEATURE [Part::Box] Box711  label="Krychle711"
  AttacherType = Attacher::AttachEngine3D
  Height = 27
  Length = 50
  Placement = pos=(-25,15,-3) rot=(0,0,1;0rad)
  Width = 32
FEATURE [Part::Cylinder] Cylinder1793  label="Válec1793"
  Angle = 360
  AttacherType = Attacher::AttachEngine3D
  Height = 32
  Placement = pos=(0,0,-3) rot=(0,0,1;0rad)
  Radius = 35
FEATURE [Part::Cylinder] Cylinder1800  label="Válec1800"
  Angle = 360
  AttacherType = Attacher::AttachEngine3D
  Height = 16
  Placement = pos=(16,42,17) rot=(0,1,0;1.5708rad)
  Radius = 4
FEATURE [Part::Box] Box712  label="Krychle712"
  AttacherType = Attacher::AttachEngine3D
  Height = 28
  Length = 20.4
  Placement = pos=(-10.2,20,-3) rot=(0,0,1;0rad)
  Width = 27
FEATURE [Part::Cut] Cut524
  Base = -> Box711
  Tool = -> Box712
FEATURE [Part::Cut] Cut527
  Base = -> Cut524
  Placement = pos=(0,0,-1) rot=(0,0,1;0rad)
  Tool = -> Cylinder1793
FEATURE [Part::Cylinder] Cylinder1796  label="Válec1796"
  Angle = 360
  AttacherType = Attacher::AttachEngine3D
  Height = 64
  Placement = pos=(-32,42,17) rot=(0,1,0;1.5708rad)
  Radius = 1.5
FEATURE [Part::Compound] Compound891
  Links = -> [Cylinder1795,Cylinder1796]
FEATURE [Part::Cylinder] Cylinder1797  label="Válec1797"
  Angle = 360
  AttacherType = Attacher::AttachEngine3D
  Height = 16
  Placement = pos=(-32,42,1) rot=(0,1,0;1.5708rad)
  Radius = 4
FEATURE [Part::Cylinder] Cylinder1799  label="Válec1799"
  Angle = 360
  AttacherType = Attacher::AttachEngine3D
  Height = 16
  Placement = pos=(16,42,1) rot=(0,1,0;1.5708rad)
  Radius = 4
FEATURE [Part::Compound] Compound892
  Links = -> [Cylinder1797,Cylinder1800,Cylinder1799,Cylinder1798]
FEATURE [Part::Cut] Cut528
  Base = -> Cut527
  Tool = -> Compound892
FEATURE [Part::Cut] Cut529
  Base = -> Cut528
  Tool = -> Compound891
FEATURE [Part::Compound] Compound896  label="G-midi_bear-hold-encoder-rear"
  Links = -> [Cut529,Compound889]
  Placement = pos=(152,62,17) rot=(0.57735,-0.57735,-0.57735;4.18879rad)
FEATURE [Mesh::Feature] Mesh001  label="G-midi_bear-hold-encoder-rear (Meshed)"
FEATURE [Part::FeaturePython] Tube001  # WARN: FeaturePython — macro-defined, semantics opaque (R4)
  AttacherType = Attacher::AttachEngine3D
  Height = 64
  InnerRadius = 12
  OuterRadius = 16
  Placement = pos=(75,16,42) rot=(1,0,0;1.5708rad)
FEATURE [Part::Cylinder] Cylinder497  label="Válec497"
  Angle = 360
  AttacherType = Attacher::AttachEngine3D
  Height = 20
  Placement = pos=(58,11,26) rot=(0,0,1;0rad)
  Radius = 1.25
FEATURE [Part::Cylinder] Cylinder498  label="Válec498"
  Angle = 360
  AttacherType = Attacher::AttachEngine3D
  Height = 20
  Placement = pos=(58,-43,26) rot=(0,0,1;0rad)
  Radius = 1.25
FEATURE [Part::Cylinder] Cylinder499  label="Válec499"
  Angle = 360
  AttacherType = Attacher::AttachEngine3D
  Height = 20
  Placement = pos=(58,-43,26) rot=(0,0,1;0rad)
  Radius = 1.25
FEATURE [Part::Cylinder] Cylinder500  label="Válec500"
  Angle = 360
  AttacherType = Attacher::AttachEngine3D
  Height = 3
  Placement = pos=(58,11,26) rot=(0,0,1;0rad)
  Radius = 2.5
FEATURE [Part::Cylinder] Cylinder501  label="Válec501"
  Angle = 360
  AttacherType = Attacher::AttachEngine3D
  Height = 3
  Placement = pos=(58,-43,26) rot=(0,0,1;0rad)
  Radius = 2.5
FEATURE [Part::Cylinder] Cylinder502  label="Válec502"
  Angle = 360
  AttacherType = Attacher::AttachEngine3D
  Height = 3
  Placement = pos=(58,-43,26) rot=(0,0,1;0rad)
  Radius = 2.5
FEATURE [Part::Cylinder] Cylinder503  label="Válec503"
  Angle = 360
  AttacherType = Attacher::AttachEngine3D
  Height = 3
  Placement = pos=(58,11,26) rot=(0,0,1;0rad)
  Radius = 2.5
FEATURE [Part::Cylinder] Cylinder504  label="Válec504"
  Angle = 360
  AttacherType = Attacher::AttachEngine3D
  Height = 20
  Placement = pos=(58,11,26) rot=(0,0,1;0rad)
  Radius = 1.25
FEATURE [Part::Box] Box215  label="Krychle215"
  AttacherType = Attacher::AttachEngine3D
  Height = 4
  Length = 40
  Placement = pos=(55,-48,37) rot=(0,0,1;0rad)
  Width = 64
FEATURE [Part::Cylinder] Cylinder505  label="Válec505"
  Angle = 360
  AttacherType = Attacher::AttachEngine3D
  Height = 64
  Placement = pos=(75,16,42) rot=(1,0,0;1.5708rad)
  Radius = 14
FEATURE [Part::Box] Box  label="Krychle"
  AttacherType = Attacher::AttachEngine3D
  Height = 100
  Length = 100
  Placement = pos=(32,-54,-63) rot=(0,0,1;0rad)
  Width = 100
FEATURE [Part::Cut] Cut378
  Base = -> Box215
  Tool = -> Cylinder505
FEATURE [Part::Compound] Compound605
  Links = -> [Cylinder503,Cylinder502]
  Placement = pos=(34,0,13) rot=(0,0,1;0rad)
FEATURE [Part::Compound] Compound606
  Links = -> [Cylinder500,Cylinder501]
  Placement = pos=(0,0,13) rot=(0,0,1;0rad)
FEATURE [Part::Compound] Compound607
  Links = -> [Compound606,Compound605]
FEATURE [Part::Chamfer] Chamfer003
  Base = -> Tube001
  Edges = 2 edges r=2: [Edge1,Edge3]
FEATURE [Part::Cut] Cut381
  Base = -> Chamfer003
  Tool = -> Box
FEATURE [Part::Compound] Compound608
  Links = -> [Cylinder497,Cylinder498]
FEATURE [Part::Compound] Compound610
  Links = -> [Cylinder504,Cylinder499]
  Placement = pos=(34,0,0) rot=(0,0,1;0rad)
FEATURE [Part::Compound] Compound609
  Links = -> [Compound608,Compound610]
FEATURE [Part::Cut] Cut379
  Base = -> Cut378
  Tool = -> Compound609
FEATURE [Part::Cut] Cut380
  Base = -> Cut379
  Tool = -> Compound607
FEATURE [Part::Chamfer] Chamfer004
  Base = -> Cut380
  Edges = 2 edges r=4: [Edge1,Edge26]
FEATURE [Part::Chamfer] Chamfer005
  Base = -> Chamfer004
  Edges = 2 edges r=4: [Edge4,Edge46]
FEATURE [Part::Compound] Compound611  label="G-midi_cable-organizer-long-old"
  Links = -> [Chamfer005,Cut381]
  Placement = pos=(0,32,0) rot=(0,0,1;0rad)
FEATURE [Part::Cylinder] Cylinder491  label="Válec491"
  Angle = 360
  AttacherType = Attacher::AttachEngine3D
  Height = 20
  Placement = pos=(58,11,26) rot=(0,0,1;0rad)
  Radius = 1.25
FEATURE [Part::Cylinder] Cylinder496  label="Válec496"
  Angle = 360
  AttacherType = Attacher::AttachEngine3D
  Height = 3
  Placement = pos=(58,11,26) rot=(0,0,1;0rad)
  Radius = 2.5
FEATURE [Part::Cylinder] Cylinder495  label="Válec495"
  Angle = 360
  AttacherType = Attacher::AttachEngine3D
  Height = 3
  Placement = pos=(58,-19,26) rot=(0,0,1;0rad)
  Radius = 2.5
FEATURE [Part::Cylinder] Cylinder494  label="Válec494"
  Angle = 360
  AttacherType = Attacher::AttachEngine3D
  Height = 3
  Placement = pos=(58,-19,26) rot=(0,0,1;0rad)
  Radius = 2.5
FEATURE [Part::Cylinder] Cylinder493  label="Válec493"
  Angle = 360
  AttacherType = Attacher::AttachEngine3D
  Height = 3
  Placement = pos=(58,11,26) rot=(0,0,1;0rad)
  Radius = 2.5
FEATURE [Part::Box] Box713  label="Krychle713"
  AttacherType = Attacher::AttachEngine3D
  Height = 100
  Length = 100
  Placement = pos=(32,-54,-63) rot=(0,0,1;0rad)
  Width = 100
FEATURE [Part::Cylinder] Cylinder492  label="Válec492"
  Angle = 360
  AttacherType = Attacher::AttachEngine3D
  Height = 20
  Placement = pos=(58,-19,26) rot=(0,0,1;0rad)
  Radius = 1.25
FEATURE [Part::Cylinder] Cylinder490  label="Válec490"
  Angle = 360
  AttacherType = Attacher::AttachEngine3D
  Height = 20
  Placement = pos=(58,-19,26) rot=(0,0,1;0rad)
  Radius = 1.25
FEATURE [Part::Cylinder] Cylinder489  label="Válec489"
  Angle = 360
  AttacherType = Attacher::AttachEngine3D
  Height = 20
  Placement = pos=(58,11,26) rot=(0,0,1;0rad)
  Radius = 1.25
FEATURE [Part::Box] Box214  label="Krychle214"
  AttacherType = Attacher::AttachEngine3D
  Height = 4
  Length = 40
  Placement = pos=(55,-24,37) rot=(0,0,1;0rad)
  Width = 40
FEATURE [Part::Cylinder] Cylinder1801  label="Válec1801"
  Angle = 360
  AttacherType = Attacher::AttachEngine3D
  Height = 40
  Placement = pos=(75,16,42) rot=(1,0,0;1.5708rad)
  Radius = 14
FEATURE [Part::Cut] Cut531
  Base = -> Box214
  Tool = -> Cylinder1801
FEATURE [Part::Compound] Compound601
  Links = -> [Cylinder496,Cylinder495]
  Placement = pos=(34,0,13) rot=(0,0,1;0rad)
FEATURE [Part::Compound] Compound600
  Links = -> [Cylinder493,Cylinder494]
  Placement = pos=(0,0,13) rot=(0,0,1;0rad)
FEATURE [Part::Compound] Compound603
  Links = -> [Compound600,Compound601]
FEATURE [Part::Compound] Compound897
  Links = -> [Cylinder489,Cylinder490]
FEATURE [Part::Compound] Compound599
  Links = -> [Cylinder491,Cylinder492]
  Placement = pos=(34,0,0) rot=(0,0,1;0rad)
FEATURE [Part::Compound] Compound602
  Links = -> [Compound897,Compound599]
FEATURE [Part::Cut] Cut376
  Base = -> Cut531
  Tool = -> Compound602
FEATURE [Part::Cut] Cut377
  Base = -> Cut376
  Tool = -> Compound603
FEATURE [Part::Chamfer] Chamfer056
  Base = -> Cut377
  Edges = 4 edges r=4: [Edge1,Edge3,Edge26,Edge35]
FEATURE [Part::FeaturePython] Tube  # WARN: FeaturePython — macro-defined, semantics opaque (R4)
  AttacherType = Attacher::AttachEngine3D
  Height = 40
  InnerRadius = 12
  OuterRadius = 16
  Placement = pos=(75,16,42) rot=(1,0,0;1.5708rad)
FEATURE [Part::Chamfer] Chamfer002
  Base = -> Tube
  Edges = 2 edges r=2: [Edge1,Edge3]
FEATURE [Part::Cut] Cut530
  Base = -> Chamfer002
  Tool = -> Box713
FEATURE [Part::Compound] Compound604  label="G-midi_cable-organizer-short-old"
  Links = -> [Chamfer056,Cut530]
FEATURE [Part::Cylinder] Cylinder1806  label="Válec1806"
  Angle = 360
  AttacherType = Attacher::AttachEngine3D
  Height = 30
  Placement = pos=(58,11,26) rot=(0,0,1;0rad)
  Radius = 2.5
FEATURE [Part::Cylinder] Cylinder1807  label="Válec1807"
  Angle = 360
  AttacherType = Attacher::AttachEngine3D
  Height = 30
  Placement = pos=(58,-19,26) rot=(0,0,1;0rad)
  Radius = 2.5
FEATURE [Part::Cylinder] Cylinder1808  label="Válec1808"
  Angle = 360
  AttacherType = Attacher::AttachEngine3D
  Height = 30
  Placement = pos=(58,-19,26) rot=(0,0,1;0rad)
  Radius = 2.5
FEATURE [Part::Cylinder] Cylinder1809  label="Válec1809"
  Angle = 360
  AttacherType = Attacher::AttachEngine3D
  Height = 30
  Placement = pos=(58,11,26) rot=(0,0,1;0rad)
  Radius = 2.5
FEATURE [Part::FeaturePython] Tube089  # WARN: FeaturePython — macro-defined, semantics opaque (R4)
  AttacherType = Attacher::AttachEngine3D
  Height = 64
  InnerRadius = 12
  OuterRadius = 16
  Placement = pos=(75,16,42) rot=(1,0,0;1.5708rad)
FEATURE [Part::Chamfer] Chamfer060
  Base = -> Tube089
  Edges = 2 edges r=2: [Edge1,Edge3]
FEATURE [Part::Cylinder] Cylinder1810  label="Válec1810"
  Angle = 360
  AttacherType = Attacher::AttachEngine3D
  Height = 20
  Placement = pos=(58,-43,26) rot=(0,0,1;0rad)
  Radius = 1.25
FEATURE [Part::Cylinder] Cylinder1811  label="Válec1811"
  Angle = 360
  AttacherType = Attacher::AttachEngine3D
  Height = 20
  Placement = pos=(58,-43,26) rot=(0,0,1;0rad)
  Radius = 1.25
FEATURE [Part::Cylinder] Cylinder1812  label="Válec1812"
  Angle = 360
  AttacherType = Attacher::AttachEngine3D
  Height = 3
  Placement = pos=(58,11,26) rot=(0,0,1;0rad)
  Radius = 2.5
FEATURE [Part::Cylinder] Cylinder1813  label="Válec1813"
  Angle = 360
  AttacherType = Attacher::AttachEngine3D
  Height = 20
  Placement = pos=(58,11,26) rot=(0,0,1;0rad)
  Radius = 1.25
FEATURE [Part::Compound] Compound903
  Links = -> [Cylinder1813,Cylinder1810]
FEATURE [Part::Cylinder] Cylinder1814  label="Válec1814"
  Angle = 360
  AttacherType = Attacher::AttachEngine3D
  Height = 3
  Placement = pos=(58,-43,26) rot=(0,0,1;0rad)
  Radius = 2.5
FEATURE [Part::Compound] Compound902
  Links = -> [Cylinder1812,Cylinder1814]
  Placement = pos=(0,0,13) rot=(0,0,1;0rad)
FEATURE [Part::Cylinder] Cylinder1815  label="Válec1815"
  Angle = 360
  AttacherType = Attacher::AttachEngine3D
  Height = 3
  Placement = pos=(58,-43,26) rot=(0,0,1;0rad)
  Radius = 2.5
FEATURE [Part::Cylinder] Cylinder1816  label="Válec1816"
  Angle = 360
  AttacherType = Attacher::AttachEngine3D
  Height = 3
  Placement = pos=(58,11,26) rot=(0,0,1;0rad)
  Radius = 2.5
FEATURE [Part::Compound] Compound904
  Links = -> [Cylinder1816,Cylinder1815]
  Placement = pos=(34,0,13) rot=(0,0,1;0rad)
FEATURE [Part::Compound] Compound905
  Links = -> [Compound902,Compound904]
FEATURE [Part::Cylinder] Cylinder1817  label="Válec1817"
  Angle = 360
  AttacherType = Attacher::AttachEngine3D
  Height = 20
  Placement = pos=(58,11,26) rot=(0,0,1;0rad)
  Radius = 1.25
FEATURE [Part::Compound] Compound900
  Links = -> [Cylinder1817,Cylinder1811]
  Placement = pos=(34,0,0) rot=(0,0,1;0rad)
FEATURE [Part::Compound] Compound901
  Links = -> [Compound903,Compound900]
FEATURE [Part::Box] Box714  label="Krychle714"
  AttacherType = Attacher::AttachEngine3D
  Height = 4
  Length = 40
  Placement = pos=(55,-48,37) rot=(0,0,1;0rad)
  Width = 64
FEATURE [Part::Cylinder] Cylinder1818  label="Válec1818"
  Angle = 360
  AttacherType = Attacher::AttachEngine3D
  Height = 64
  Placement = pos=(75,16,42) rot=(1,0,0;1.5708rad)
  Radius = 14
FEATURE [Part::Box] Box715  label="Krychle715"
  AttacherType = Attacher::AttachEngine3D
  Height = 100
  Length = 100
  Placement = pos=(32,-54,-63) rot=(0,0,1;0rad)
  Width = 100
FEATURE [Part::Cylinder] Cylinder1819  label="Válec1819"
  Angle = 360
  AttacherType = Attacher::AttachEngine3D
  Height = 20
  Placement = pos=(58,11,26) rot=(0,0,1;0rad)
  Radius = 1.25
FEATURE [Part::Cylinder] Cylinder1820  label="Válec1820"
  Angle = 360
  AttacherType = Attacher::AttachEngine3D
  Height = 3
  Placement = pos=(58,11,26) rot=(0,0,1;0rad)
  Radius = 2.5
FEATURE [Part::Cylinder] Cylinder1821  label="Válec1821"
  Angle = 360
  AttacherType = Attacher::AttachEngine3D
  Height = 3
  Placement = pos=(58,-19,26) rot=(0,0,1;0rad)
  Radius = 2.5
FEATURE [Part::Compound] Compound899
  Links = -> [Cylinder1820,Cylinder1821]
  Placement = pos=(34,0,13) rot=(0,0,1;0rad)
FEATURE [Part::Cylinder] Cylinder1822  label="Válec1822"
  Angle = 360
  AttacherType = Attacher::AttachEngine3D
  Height = 3
  Placement = pos=(58,-19,26) rot=(0,0,1;0rad)
  Radius = 2.5
FEATURE [Part::Cylinder] Cylinder1823  label="Válec1823"
  Angle = 360
  AttacherType = Attacher::AttachEngine3D
  Height = 3
  Placement = pos=(58,11,26) rot=(0,0,1;0rad)
  Radius = 2.5
FEATURE [Part::Compound] Compound909
  Links = -> [Cylinder1823,Cylinder1822]
  Placement = pos=(0,0,13) rot=(0,0,1;0rad)
FEATURE [Part::Compound] Compound908
  Links = -> [Compound909,Compound899]
FEATURE [Part::Box] Box716  label="Krychle716"
  AttacherType = Attacher::AttachEngine3D
  Height = 100
  Length = 100
  Placement = pos=(32,-54,-63) rot=(0,0,1;0rad)
  Width = 100
FEATURE [Part::Cylinder] Cylinder1824  label="Válec1824"
  Angle = 360
  AttacherType = Attacher::AttachEngine3D
  Height = 20
  Placement = pos=(58,-19,26) rot=(0,0,1;0rad)
  Radius = 1.25
FEATURE [Part::Compound] Compound898
  Links = -> [Cylinder1819,Cylinder1824]
  Placement = pos=(34,0,0) rot=(0,0,1;0rad)
FEATURE [Part::Cylinder] Cylinder1825  label="Válec1825"
  Angle = 360
  AttacherType = Attacher::AttachEngine3D
  Height = 20
  Placement = pos=(58,-19,26) rot=(0,0,1;0rad)
  Radius = 1.25
FEATURE [Part::Cylinder] Cylinder1826  label="Válec1826"
  Angle = 360
  AttacherType = Attacher::AttachEngine3D
  Height = 20
  Placement = pos=(58,11,26) rot=(0,0,1;0rad)
  Radius = 1.25
FEATURE [Part::Compound] Compound907
  Links = -> [Cylinder1826,Cylinder1825]
FEATURE [Part::Compound] Compound906
  Links = -> [Compound907,Compound898]
FEATURE [Part::Box] Box717  label="Krychle717"
  AttacherType = Attacher::AttachEngine3D
  Height = 4
  Length = 40
  Placement = pos=(55,-24,37) rot=(0,0,1;0rad)
  Width = 40
FEATURE [Part::Cylinder] Cylinder1827  label="Válec1827"
  Angle = 360
  AttacherType = Attacher::AttachEngine3D
  Height = 40
  Placement = pos=(75,16,42) rot=(1,0,0;1.5708rad)
  Radius = 14
FEATURE [Part::Cylinder] Cylinder1802  label="Válec1802"
  Angle = 360
  AttacherType = Attacher::AttachEngine3D
  Height = 30
  Placement = pos=(58,11,26) rot=(0,0,1;0rad)
  Radius = 2.5
FEATURE [Part::Cylinder] Cylinder1803  label="Válec1803"
  Angle = 360
  AttacherType = Attacher::AttachEngine3D
  Height = 30
  Placement = pos=(58,-43,26) rot=(0,0,1;0rad)
  Radius = 2.5
FEATURE [Part::Cylinder] Cylinder1804  label="Válec1804"
  Angle = 360
  AttacherType = Attacher::AttachEngine3D
  Height = 30
  Placement = pos=(58,-43,26) rot=(0,0,1;0rad)
  Radius = 2.5
FEATURE [Part::Cylinder] Cylinder1805  label="Válec1805"
  Angle = 360
  AttacherType = Attacher::AttachEngine3D
  Height = 30
  Placement = pos=(58,11,26) rot=(0,0,1;0rad)
  Radius = 2.5
FEATURE [Part::Cut] Cut535
  Base = -> Chamfer060
  Tool = -> Box715
FEATURE [Part::Cut] Cut536
  Base = -> Box714
  Tool = -> Cylinder1818
FEATURE [Part::Cut] Cut534
  Base = -> Cut536
  Tool = -> Compound901
FEATURE [Part::Cut] Cut537
  Base = -> Cut534
  Tool = -> Compound905
FEATURE [Part::Chamfer] Chamfer061
  Base = -> Cut537
  Edges = 2 edges r=4: [Edge1,Edge26]
FEATURE [Part::Chamfer] Chamfer059
  Base = -> Chamfer061
  Edges = 2 edges r=4: [Edge4,Edge46]
FEATURE [Part::Cut] Cut538
  Base = -> Box717
  Tool = -> Cylinder1827
FEATURE [Part::Cut] Cut539
  Base = -> Cut538
  Tool = -> Compound906
FEATURE [Part::Cut] Cut540
  Base = -> Cut539
  Tool = -> Compound908
FEATURE [Part::Chamfer] Chamfer058
  Base = -> Cut540
  Edges = 4 edges r=4: [Edge1,Edge3,Edge26,Edge35]
FEATURE [Part::FeaturePython] Tube090  # WARN: FeaturePython — macro-defined, semantics opaque (R4)
  AttacherType = Attacher::AttachEngine3D
  Height = 40
  InnerRadius = 12
  OuterRadius = 16
  Placement = pos=(75,16,42) rot=(1,0,0;1.5708rad)
FEATURE [Part::Chamfer] Chamfer057
  Base = -> Tube090
  Edges = 2 edges r=2: [Edge1,Edge3]
FEATURE [Part::Cut] Cut533
  Base = -> Chamfer057
  Tool = -> Box716
FEATURE [Part::Compound] Compound910
  Links = -> [Cylinder1802,Cylinder1803]
  Placement = pos=(0,0,13) rot=(0,0,1;0rad)
FEATURE [Part::Compound] Compound911
  Links = -> [Cylinder1805,Cylinder1804]
  Placement = pos=(34,0,13) rot=(0,0,1;0rad)
FEATURE [Part::Compound] Compound912
  Links = -> [Compound910,Compound911]
FEATURE [Part::Cut] Cut532
  Base = -> Cut535
  Tool = -> Compound912
FEATURE [Part::Compound] Compound913  label="G-midi_cable-organizer-long"
  Links = -> [Chamfer059,Cut532]
FEATURE [Part::Compound] Compound914
  Links = -> [Cylinder1806,Cylinder1807]
  Placement = pos=(34,0,13) rot=(0,0,1;0rad)
FEATURE [Part::Compound] Compound916
  Links = -> [Cylinder1809,Cylinder1808]
  Placement = pos=(0,0,13) rot=(0,0,1;0rad)
FEATURE [Part::Compound] Compound915
  Links = -> [Compound916,Compound914]
FEATURE [Part::Cut] Cut541
  Base = -> Cut533
  Tool = -> Compound915
FEATURE [Part::Compound] Compound917  label="G-midi_cable-organizer-short"
  Links = -> [Chamfer058,Cut541]
FEATURE [Part::FeaturePython] Tube091  # WARN: FeaturePython — macro-defined, semantics opaque (R4)
  AttacherType = Attacher::AttachEngine3D
  Height = 40
  InnerRadius = 12
  OuterRadius = 16
  Placement = pos=(75,16,42) rot=(1,0,0;1.5708rad)
FEATURE [Part::Cylinder] Cylinder1828  label="Válec1828"
  Angle = 360
  AttacherType = Attacher::AttachEngine3D
  Height = 30
  Placement = pos=(58,11,26) rot=(0,0,1;0rad)
  Radius = 2.5
FEATURE [Part::Cylinder] Cylinder1829  label="Válec1829"
  Angle = 360
  AttacherType = Attacher::AttachEngine3D
  Height = 30
  Placement = pos=(58,-19,26) rot=(0,0,1;0rad)
  Radius = 2.5
FEATURE [Part::Cylinder] Cylinder1830  label="Válec1830"
  Angle = 360
  AttacherType = Attacher::AttachEngine3D
  Height = 30
  Placement = pos=(58,-19,26) rot=(0,0,1;0rad)
  Radius = 2.5
FEATURE [Part::Cylinder] Cylinder1831  label="Válec1831"
  Angle = 360
  AttacherType = Attacher::AttachEngine3D
  Height = 30
  Placement = pos=(58,11,26) rot=(0,0,1;0rad)
  Radius = 2.5
FEATURE [Part::Cylinder] Cylinder1832  label="Válec1832"
  Angle = 360
  AttacherType = Attacher::AttachEngine3D
  Height = 20
  Placement = pos=(58,11,26) rot=(0,0,1;0rad)
  Radius = 1.25
FEATURE [Part::Cylinder] Cylinder1833  label="Válec1833"
  Angle = 360
  AttacherType = Attacher::AttachEngine3D
  Height = 3
  Placement = pos=(58,11,26) rot=(0,0,1;0rad)
  Radius = 2.5
FEATURE [Part::Cylinder] Cylinder1834  label="Válec1834"
  Angle = 360
  AttacherType = Attacher::AttachEngine3D
  Height = 3
  Placement = pos=(58,-19,26) rot=(0,0,1;0rad)
  Radius = 2.5
FEATURE [Part::Cylinder] Cylinder1835  label="Válec1835"
  Angle = 360
  AttacherType = Attacher::AttachEngine3D
  Height = 3
  Placement = pos=(58,-19,26) rot=(0,0,1;0rad)
  Radius = 2.5
FEATURE [Part::Cylinder] Cylinder1836  label="Válec1836"
  Angle = 360
  AttacherType = Attacher::AttachEngine3D
  Height = 3
  Placement = pos=(58,11,26) rot=(0,0,1;0rad)
  Radius = 2.5
FEATURE [Part::Box] Box718  label="Krychle718"
  AttacherType = Attacher::AttachEngine3D
  Height = 100
  Length = 100
  Placement = pos=(32,-54,-63) rot=(0,0,1;0rad)
  Width = 100
FEATURE [Part::Cylinder] Cylinder1837  label="Válec1837"
  Angle = 360
  AttacherType = Attacher::AttachEngine3D
  Height = 20
  Placement = pos=(58,-19,26) rot=(0,0,1;0rad)
  Radius = 1.25
FEATURE [Part::Chamfer] Chamfer062
  Base = -> Tube091
  Edges = 2 edges r=2: [Edge1,Edge3]
FEATURE [Part::Compound] Compound918
  Links = -> [Cylinder1832,Cylinder1837]
  Placement = pos=(34,0,0) rot=(0,0,1;0rad)
FEATURE [Part::Compound] Compound919
  Links = -> [Cylinder1833,Cylinder1834]
  Placement = pos=(34,0,13) rot=(0,0,1;0rad)
FEATURE [Part::Compound] Compound923
  Links = -> [Cylinder1836,Cylinder1835]
  Placement = pos=(0,0,13) rot=(0,0,1;0rad)
FEATURE [Part::Compound] Compound922
  Links = -> [Compound923,Compound919]
FEATURE [Part::Compound] Compound924
  Links = -> [Cylinder1828,Cylinder1829]
  Placement = pos=(34,0,13) rot=(0,0,1;0rad)
FEATURE [Part::Compound] Compound926
  Links = -> [Cylinder1831,Cylinder1830]
  Placement = pos=(0,0,13) rot=(0,0,1;0rad)
FEATURE [Part::Compound] Compound925
  Links = -> [Compound926,Compound924]
FEATURE [Part::Cylinder] Cylinder1838  label="Válec1838"
  Angle = 360
  AttacherType = Attacher::AttachEngine3D
  Height = 20
  Placement = pos=(58,-19,26) rot=(0,0,1;0rad)
  Radius = 1.25
FEATURE [Part::Cylinder] Cylinder1839  label="Válec1839"
  Angle = 360
  AttacherType = Attacher::AttachEngine3D
  Height = 20
  Placement = pos=(58,11,26) rot=(0,0,1;0rad)
  Radius = 1.25
FEATURE [Part::Compound] Compound921
  Links = -> [Cylinder1839,Cylinder1838]
FEATURE [Part::Compound] Compound920
  Links = -> [Compound921,Compound918]
FEATURE [Part::Box] Box719  label="Krychle719"
  AttacherType = Attacher::AttachEngine3D
  Height = 4
  Length = 40
  Placement = pos=(55,-24,37) rot=(0,0,1;0rad)
  Width = 40
FEATURE [Part::Cylinder] Cylinder1840  label="Válec1840"
  Angle = 360
  AttacherType = Attacher::AttachEngine3D
  Height = 40
  Placement = pos=(75,16,42) rot=(1,0,0;1.5708rad)
  Radius = 14
FEATURE [Part::Cut] Cut542
  Base = -> Chamfer062
  Tool = -> Box718
FEATURE [Part::Cut] Cut543
  Base = -> Box719
  Tool = -> Cylinder1840
FEATURE [Part::Cut] Cut544
  Base = -> Cut543
  Tool = -> Compound920
FEATURE [Part::Cut] Cut545
  Base = -> Cut544
  Tool = -> Compound922
FEATURE [Part::Chamfer] Chamfer063
  Base = -> Cut545
  Edges = 4 edges r=4: [Edge1,Edge3,Edge26,Edge35]
FEATURE [Part::Cut] Cut546
  Base = -> Cut542
  Tool = -> Compound925
FEATURE [Part::Compound] Compound927  label="G-midi_cable-organizer-short001"
  Links = -> [Chamfer063,Cut546]
  Placement = pos=(105.626,43.8637,-59) rot=(0.395424,0.829023,0.395424;4.52597rad)
